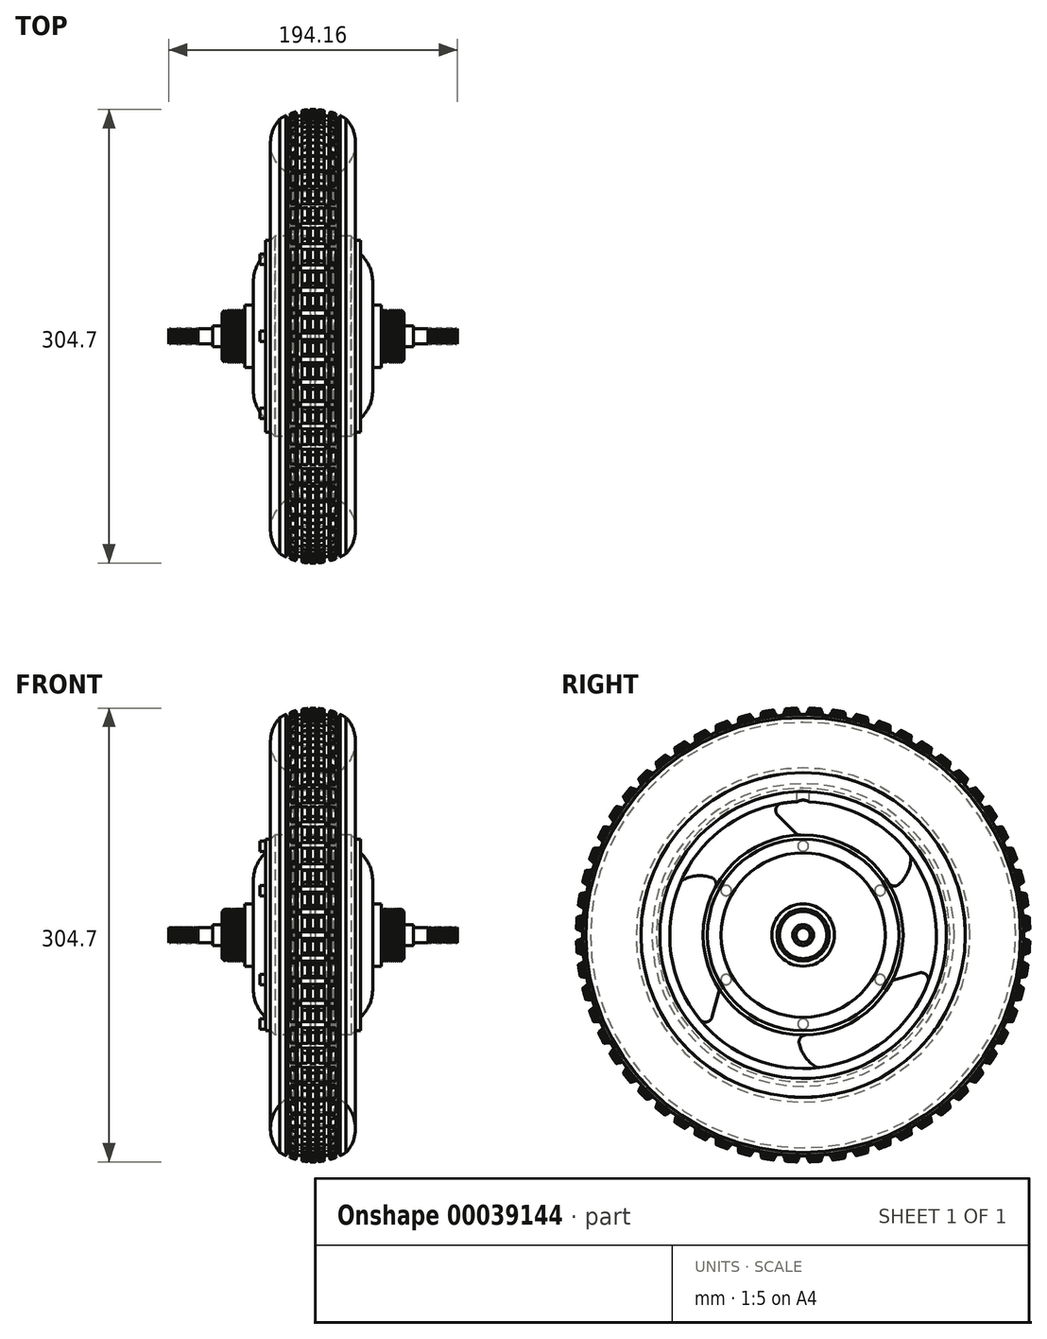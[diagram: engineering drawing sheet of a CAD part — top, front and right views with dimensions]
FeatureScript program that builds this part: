
annotation { "Feature Type Name" : "Feature", "Feature Type Description" : "" }
export const myFeature = defineFeature(function(context is Context, id is Id, definition is map)
    precondition{}
    {
        {
            var Q0;
            Q0=qCreatedBy(makeId("Front.planeOp"),FACE);
            var sketch = newSketch(context, id + "F0", { "sketchPlane" : qUnion([Q0])});
            skArc(sketch, "E0", {"start": v(0, 96.9) * mm, "mid": v(6.4, 97.33) * mm, "end": v(12.7, 98.63) * mm});
            skArc(sketch, "E1", {"start": v(18, 106.35) * mm, "mid": v(15.35, 109) * mm, "end": v(12.7, 106.35) * mm});
            skLineSegment(sketch, "E2", {"start": v(18, 106.35) * mm, "end": v(18, 96.3) * mm});
            skLineSegment(sketch, "E3", {"start": v(15.35, 109) * mm, "end": v(0, 109) * mm, "construction": true});
            skLineSegment(sketch, "E4", {"start": v(0, 0) * mm, "end": v(97.08, 0) * mm});
            skLineSegment(sketch, "E5", {"start": v(0, 0) * mm, "end": v(0, 109) * mm, "construction": true});
            skLineSegment(sketch, "E6", {"start": v(0, 96.9) * mm, "end": v(18, 96.9) * mm, "construction": true});
            skLineSegment(sketch, "E7", {"start": v(12.7, 98.63) * mm, "end": v(12.7, 106.35) * mm});
            skLineSegment(sketch, "E8", {"start": v(1.59, 67.19) * mm, "end": v(25.67, 67.19) * mm});
            skLineSegment(sketch, "E9", {"start": v(25.67, 67.19) * mm, "end": v(28.53, 64.33) * mm});
            skLineSegment(sketch, "E10", {"start": v(28.53, 64.33) * mm, "end": v(31.85, 64.33) * mm});
            skLineSegment(sketch, "E11", {"start": v(31.85, 64.33) * mm, "end": v(31.85, 55.2) * mm});
            skArc(sketch, "E12", {"start": v(40.1, 36.45) * mm, "mid": v(37.95, 46.7) * mm, "end": v(31.85, 55.2) * mm});
            skLineSegment(sketch, "E13", {"start": v(40.1, 36.45) * mm, "end": v(40.1, 20.94) * mm});
            skLineSegment(sketch, "E14", {"start": v(40.1, 20.94) * mm, "end": v(46, 20.94) * mm});
            skLineSegment(sketch, "E15", {"start": v(46, 20.94) * mm, "end": v(46, 17.46) * mm});
            skLineSegment(sketch, "E16", {"start": v(46, 17.46) * mm, "end": v(61, 17.46) * mm});
            skLineSegment(sketch, "E17", {"start": v(61, 17.46) * mm, "end": v(61, 7) * mm});
            skLineSegment(sketch, "E18", {"start": v(61, 7) * mm, "end": v(67.58, 7) * mm});
            skLineSegment(sketch, "E19", {"start": v(67.58, 7) * mm, "end": v(67.58, 5) * mm});
            skLineSegment(sketch, "E20", {"start": v(67.58, 5) * mm, "end": v(97.08, 5) * mm});
            skLineSegment(sketch, "E21", {"start": v(97.08, 5) * mm, "end": v(97.08, 0) * mm});
            skLineSegment(sketch, "E22", {"start": v(18, 96.3) * mm, "end": v(1.59, 89.65) * mm});
            skLineSegment(sketch, "E23", {"start": v(1.59, 89.65) * mm, "end": v(1.59, 67.18) * mm});
            skLineSegment(sketch, "E24.MirrorCS", {"start": v(-25.67, 67.18) * mm, "end": v(-28.53, 64.33) * mm});
            skLineSegment(sketch, "E25.MirrorCS", {"start": v(-67.58, 7) * mm, "end": v(-67.58, 5) * mm});
            skLineSegment(sketch, "E26.MirrorCS", {"start": v(-61, 7) * mm, "end": v(-67.58, 7) * mm});
            skLineSegment(sketch, "E27.MirrorCS", {"start": v(-12.7, 98.63) * mm, "end": v(-12.7, 106.35) * mm});
            skLineSegment(sketch, "E28.MirrorCS", {"start": v(-97.08, 5) * mm, "end": v(-97.08, 0) * mm});
            skLineSegment(sketch, "E29.MirrorCS", {"start": v(-40.1, 20.94) * mm, "end": v(-46, 20.94) * mm});
            skLineSegment(sketch, "E30.MirrorCS", {"start": v(-28.53, 64.33) * mm, "end": v(-31.85, 64.33) * mm});
            skLineSegment(sketch, "E31.MirrorCS", {"start": v(-46, 20.94) * mm, "end": v(-46, 17.46) * mm});
            skLineSegment(sketch, "E32.MirrorCS", {"start": v(-46, 17.46) * mm, "end": v(-61, 17.46) * mm});
            skLineSegment(sketch, "E33.MirrorCS", {"start": v(0, 96.9) * mm, "end": v(-18, 96.9) * mm, "construction": true});
            skLineSegment(sketch, "E34.MirrorCS", {"start": v(-18, 106.35) * mm, "end": v(-18, 96.3) * mm});
            skLineSegment(sketch, "E35.MirrorCS", {"start": v(-40.1, 36.45) * mm, "end": v(-40.1, 20.94) * mm});
            skArc(sketch, "E36.MirrorCS", {"start": v(-18, 106.35) * mm, "mid": v(-15.35, 109) * mm, "end": v(-12.7, 106.35) * mm});
            skLineSegment(sketch, "E37.MirrorCS", {"start": v(-61, 17.46) * mm, "end": v(-61, 7) * mm});
            skLineSegment(sketch, "E38.MirrorCS", {"start": v(-15.35, 109) * mm, "end": v(0, 109) * mm, "construction": true});
            skLineSegment(sketch, "E39.MirrorCS", {"start": v(0, 0) * mm, "end": v(-97.08, 0) * mm});
            skLineSegment(sketch, "E40.MirrorCS", {"start": v(-1.59, 67.19) * mm, "end": v(-25.67, 67.19) * mm});
            skLineSegment(sketch, "E41.MirrorCS", {"start": v(-18, 96.3) * mm, "end": v(-1.59, 89.65) * mm});
            skLineSegment(sketch, "E42.MirrorCS", {"start": v(-31.85, 64.33) * mm, "end": v(-31.85, 55.2) * mm});
            skLineSegment(sketch, "E43.MirrorCS", {"start": v(-1.59, 89.65) * mm, "end": v(-1.59, 67.18) * mm});
            skArc(sketch, "E44.MirrorCS", {"start": v(0, 96.9) * mm, "mid": v(-6.4, 97.33) * mm, "end": v(-12.7, 98.63) * mm});
            skLineSegment(sketch, "E45.MirrorCS", {"start": v(-67.58, 5) * mm, "end": v(-97.08, 5) * mm});
            skArc(sketch, "E46.MirrorCS", {"start": v(-40.1, 36.45) * mm, "mid": v(-37.95, 46.7) * mm, "end": v(-31.85, 55.2) * mm});
            skSolve(sketch);
        }
        {
            var Q0;
            Q0 = qSketchRegion(id + "F0", true);
            var Q1;
            Q1=sQuery(id+"F0.wireOp",EDGE,"E4");
            revolve(context, id + "F1", {"entities" : qUnion([Q0]), "axis" : qUnion([Q1]), "revolveType" : RevolveType.FULL});
        }
        {
            var Q0;
            Q0=makeQuery(id+"F1.opRevolve","SWEPT_FACE",FACE,{"disambiguationData":[OSD([sQuery(id+"F0.wireOp",EDGE,"E23")])]});
            var sketch = newSketch(context, id + "F2", { "sketchPlane" : qUnion([Q0])});
            skArc(sketch, "E47.0", {"start": v(-56.44, 36.45) * mm, "mid": v(-67.18, -0.2) * mm, "end": v(-56.23, -36.78) * mm});
            skArc(sketch, "E48.1", {"start": v(-63.4, -63.4) * mm, "mid": v(-88.15, -16.34) * mm, "end": v(-81.9, 36.45) * mm});
            skLineSegment(sketch, "E49", {"start": v(-36.5, 36.45) * mm, "end": v(-81.9, 36.45) * mm, "construction": true});
            skLineSegment(sketch, "E50", {"start": v(-63.4, -63.4) * mm, "end": v(-36.5, 36.45) * mm, "construction": true});
            skLineSegment(sketch, "E51", {"start": v(0, 0) * mm, "end": v(-63.4, -63.4) * mm, "construction": true});
            skArc(sketch, "E52", {"start": v(-56.44, 36.45) * mm, "mid": v(-69.17, 39.87) * mm, "end": v(-81.9, 36.45) * mm});
            skLineSegment(sketch, "E53", {"start": v(-63.4, -63.4) * mm, "end": v(-56.23, -36.78) * mm});
            skLineSegment(sketch, "E54.1.0", {"start": v(86.6, -23.2) * mm, "end": v(59.96, -30.3) * mm});
            skArc(sketch, "E54.1.1", {"start": v(-3.35, -67.1) * mm, "mid": v(0.06, -79.84) * mm, "end": v(9.39, -89.16) * mm});
            skArc(sketch, "E54.1.2", {"start": v(86.6, -23.2) * mm, "mid": v(58.23, -68.17) * mm, "end": v(9.39, -89.16) * mm});
            skArc(sketch, "E54.1.3", {"start": v(-3.35, -67.1) * mm, "mid": v(33.76, -58.09) * mm, "end": v(59.96, -30.3) * mm});
            skArc(sketch, "E54.1.4", {"start": v(-3.35, -67.1) * mm, "mid": v(33.76, -58.09) * mm, "end": v(59.96, -30.3) * mm});
            skLineSegment(sketch, "E54.2.0", {"start": v(-23.2, 86.6) * mm, "end": v(-3.74, 67.08) * mm});
            skArc(sketch, "E54.2.1", {"start": v(59.79, 30.65) * mm, "mid": v(69.12, 39.97) * mm, "end": v(72.52, 52.7) * mm});
            skArc(sketch, "E54.2.2", {"start": v(-23.2, 86.6) * mm, "mid": v(29.92, 84.51) * mm, "end": v(72.52, 52.7) * mm});
            skArc(sketch, "E54.2.3", {"start": v(59.79, 30.65) * mm, "mid": v(33.42, 58.28) * mm, "end": v(-3.74, 67.08) * mm});
            skArc(sketch, "E54.2.4", {"start": v(59.79, 30.65) * mm, "mid": v(33.42, 58.28) * mm, "end": v(-3.74, 67.08) * mm});
            skSolve(sketch);
        }
        {
            var Q0;
            Q0 = qSketchRegion(id + "F2", true);
            extrude(context, id + "F3", {"entities" : qUnion([Q0]), "operationType" : NewBodyOperationType.REMOVE, "endBound" : BoundingType.THROUGH_ALL, "oppositeDirection" : true, "depth" : 25.4 * mm});
        }
        {
            var Q0;
            Q0=makeQuery(id+"F3.boolean.opBoolean","COPY",EDGE,{"derivedFrom":makeQuery(id+"F3.opExtrude","SWEPT_EDGE",EDGE,{"disambiguationData":[OSD([sQuery(id+"F0.wireOp",EDGE,"E22"),sQuery(id+"F0.wireOp",EDGE,"E23"),sQuery(id+"F2.wireOp",EDGE,"E48.1"),sQuery(id+"F2.wireOp",EDGE,"E53")])]})});
            var Q1;
            Q1=makeQuery(id+"F3.boolean.opBoolean","COPY",EDGE,{"derivedFrom":makeQuery(id+"F3.opExtrude","SWEPT_EDGE",EDGE,{"disambiguationData":[OSD([sQuery(id+"F0.wireOp",EDGE,"E8"),sQuery(id+"F0.wireOp",EDGE,"E23"),sQuery(id+"F2.wireOp",EDGE,"E47.0"),sQuery(id+"F2.wireOp",EDGE,"E53")])]})});
            var Q2;
            Q2=makeQuery(id+"F3.boolean.opBoolean","COPY",EDGE,{"derivedFrom":makeQuery(id+"F3.opExtrude","SWEPT_EDGE",EDGE,{"disambiguationData":[OSD([sQuery(id+"F0.wireOp",EDGE,"E8"),sQuery(id+"F0.wireOp",EDGE,"E23"),sQuery(id+"F2.wireOp",EDGE,"E47.0"),sQuery(id+"F2.wireOp",EDGE,"E52")])]})});
            var Q3;
            Q3=makeQuery(id+"F3.boolean.opBoolean","COPY",EDGE,{"derivedFrom":makeQuery(id+"F3.opExtrude","SWEPT_EDGE",EDGE,{"disambiguationData":[OSD([sQuery(id+"F0.wireOp",EDGE,"E22"),sQuery(id+"F0.wireOp",EDGE,"E23"),sQuery(id+"F2.wireOp",EDGE,"E48.1"),sQuery(id+"F2.wireOp",EDGE,"E52")])]})});
            var Q4;
            Q4=makeQuery(id+"F3.boolean.opBoolean","COPY",EDGE,{"derivedFrom":makeQuery(id+"F3.opExtrude","SWEPT_EDGE",EDGE,{"disambiguationData":[OSD([sQuery(id+"F0.wireOp",EDGE,"E22"),sQuery(id+"F0.wireOp",EDGE,"E23"),sQuery(id+"F2.wireOp",EDGE,"E54.1.1"),sQuery(id+"F2.wireOp",EDGE,"E54.1.2")])]})});
            var Q5;
            Q5=makeQuery(id+"F3.boolean.opBoolean","COPY",EDGE,{"derivedFrom":makeQuery(id+"F3.opExtrude","SWEPT_EDGE",EDGE,{"disambiguationData":[OSD([sQuery(id+"F0.wireOp",EDGE,"E8"),sQuery(id+"F0.wireOp",EDGE,"E23"),sQuery(id+"F2.wireOp",EDGE,"E54.1.1"),sQuery(id+"F2.wireOp",EDGE,"E54.1.4")])]})});
            var Q6;
            Q6=makeQuery(id+"F3.boolean.opBoolean","COPY",EDGE,{"derivedFrom":makeQuery(id+"F3.opExtrude","SWEPT_EDGE",EDGE,{"disambiguationData":[OSD([sQuery(id+"F0.wireOp",EDGE,"E22"),sQuery(id+"F0.wireOp",EDGE,"E23"),sQuery(id+"F2.wireOp",EDGE,"E54.1.0"),sQuery(id+"F2.wireOp",EDGE,"E54.1.2")])]})});
            var Q7;
            Q7=makeQuery(id+"F3.boolean.opBoolean","COPY",EDGE,{"derivedFrom":makeQuery(id+"F3.opExtrude","SWEPT_EDGE",EDGE,{"disambiguationData":[OSD([sQuery(id+"F0.wireOp",EDGE,"E8"),sQuery(id+"F0.wireOp",EDGE,"E23"),sQuery(id+"F2.wireOp",EDGE,"E54.1.0"),sQuery(id+"F2.wireOp",EDGE,"E54.1.4")])]})});
            var Q8;
            Q8=makeQuery(id+"F3.boolean.opBoolean","COPY",EDGE,{"derivedFrom":makeQuery(id+"F3.opExtrude","SWEPT_EDGE",EDGE,{"disambiguationData":[OSD([sQuery(id+"F0.wireOp",EDGE,"E8"),sQuery(id+"F0.wireOp",EDGE,"E23"),sQuery(id+"F2.wireOp",EDGE,"E54.2.1"),sQuery(id+"F2.wireOp",EDGE,"E54.2.4")])]})});
            var Q9;
            Q9=makeQuery(id+"F3.boolean.opBoolean","COPY",EDGE,{"derivedFrom":makeQuery(id+"F3.opExtrude","SWEPT_EDGE",EDGE,{"disambiguationData":[OSD([sQuery(id+"F0.wireOp",EDGE,"E22"),sQuery(id+"F0.wireOp",EDGE,"E23"),sQuery(id+"F2.wireOp",EDGE,"E54.2.1"),sQuery(id+"F2.wireOp",EDGE,"E54.2.2")])]})});
            var Q10;
            Q10=makeQuery(id+"F3.boolean.opBoolean","COPY",EDGE,{"derivedFrom":makeQuery(id+"F3.opExtrude","SWEPT_EDGE",EDGE,{"disambiguationData":[OSD([sQuery(id+"F0.wireOp",EDGE,"E8"),sQuery(id+"F0.wireOp",EDGE,"E23"),sQuery(id+"F2.wireOp",EDGE,"E54.2.0"),sQuery(id+"F2.wireOp",EDGE,"E54.2.4")])]})});
            var Q11;
            Q11=makeQuery(id+"F3.boolean.opBoolean","COPY",EDGE,{"derivedFrom":makeQuery(id+"F3.opExtrude","SWEPT_EDGE",EDGE,{"disambiguationData":[OSD([sQuery(id+"F0.wireOp",EDGE,"E22"),sQuery(id+"F0.wireOp",EDGE,"E23"),sQuery(id+"F2.wireOp",EDGE,"E54.2.0"),sQuery(id+"F2.wireOp",EDGE,"E54.2.2")])]})});
            fillet(context, id + "F4", {"entities" : qUnion([Q0, Q1, Q2, Q3, Q4, Q5, Q6, Q7, Q8, Q9, Q10, Q11]), "radius" : 4.76 * mm, "tangentPropagation" : true, "allowEdgeOverflow" : false});
        }
        {
            var Q0;
            Q0=qCreatedBy(makeId("Top.planeOp"),FACE);
            cPlane(context, id + "F5", {"entities" : qUnion([Q0]), "cplaneType" : CPlaneType.OFFSET, "offset" : 114.3 * mm, "width" : 152.4 * mm, "height" : 152.4 * mm});
        }
        {
            var Q0;
            Q0=qCreatedBy(id+"F5.planeOp",FACE);
            var sketch = newSketch(context, id + "F6", { "sketchPlane" : qUnion([Q0])});
            skCircle(sketch, "E55", {"center": v(0, 0) * mm, "radius": 4 * mm});
            skSolve(sketch);
        }
        {
            var Q0;
            Q0=makeQuery(id+"F6.imprint","IMPRINT",FACE,{"disambiguationData":[TD([[makeQuery(id+"F6.imprint","IMPRINT",EDGE,{"derivedFrom":sQuery(id+"F6.wireOp",EDGE,"E55")}),1.0]])]});
            extrude(context, id + "F7", {"entities" : qUnion([Q0]), "operationType" : NewBodyOperationType.REMOVE, "oppositeDirection" : true, "depth" : 38.1 * mm});
        }
        {
            var Q0;
            Q0=makeQuery(id+"F1.opRevolve","SWEPT_FACE",FACE,{"disambiguationData":[OSD([sQuery(id+"F0.wireOp",EDGE,"E42.MirrorCS")])]});
            var sketch = newSketch(context, id + "F8", { "sketchPlane" : qUnion([Q0])});
            skCircle(sketch, "E56", {"center": v(0, 59.76) * mm, "radius": 3.5 * mm});
            skLineSegment(sketch, "E57", {"start": v(0, 64.33) * mm, "end": v(0, 55.2) * mm, "construction": true});
            skCircle(sketch, "E58.1.0", {"center": v(-51.76, 29.88) * mm, "radius": 3.5 * mm});
            skCircle(sketch, "E58.2.0", {"center": v(-51.76, -29.88) * mm, "radius": 3.5 * mm});
            skCircle(sketch, "E58.3.0", {"center": v(0, -59.76) * mm, "radius": 3.5 * mm});
            skCircle(sketch, "E58.4.0", {"center": v(51.76, -29.88) * mm, "radius": 3.5 * mm});
            skCircle(sketch, "E58.5.0", {"center": v(51.76, 29.88) * mm, "radius": 3.5 * mm});
            skPoint(sketch, "E58.center", {"position": v(0, 0) * mm});
            skSolve(sketch);
        }
        {
            var Q0;
            Q0=makeQuery(id+"F1.opRevolve","SWEPT_EDGE",EDGE,{"disambiguationData":[OSD([sQuery(id+"F0.wireOp",EDGE,"E16"),sQuery(id+"F0.wireOp",EDGE,"E17")])]});
            var Q1;
            Q1=makeQuery(id+"F1.opRevolve","SWEPT_EDGE",EDGE,{"disambiguationData":[OSD([sQuery(id+"F0.wireOp",EDGE,"E32.MirrorCS"),sQuery(id+"F0.wireOp",EDGE,"E37.MirrorCS")])]});
            chamfer(context, id + "F9", {"entities" : qUnion([Q0, Q1]), "width" : 1.59 * mm, "tangentPropagation" : true});
        }
        {
            var Q0;
            Q0 = qSketchRegion(id + "F8", true);
            extrude(context, id + "F10", {"entities" : qUnion([Q0]), "operationType" : NewBodyOperationType.ADD, "depth" : 3.7 * mm});
        }
        {
            var Q0;
            Q0=qCreatedBy(makeId("Front.planeOp"),FACE);
            var sketch = newSketch(context, id + "F11", { "sketchPlane" : qUnion([Q0])});
            skLineSegment(sketch, "E59", {"start": v(12.7, 101.6) * mm, "end": v(12.7, 109) * mm});
            skLineSegment(sketch, "E60", {"start": v(12.7, 109) * mm, "end": v(15.88, 109) * mm});
            skArc(sketch, "E61", {"start": v(15.87, 109) * mm, "mid": v(28.24, 125.95) * mm, "end": v(22.23, 146.05) * mm});
            skArc(sketch, "E62", {"start": v(22.23, 146.05) * mm, "mid": v(20.29, 147.18) * mm, "end": v(18.3, 148.21) * mm});
            skLineSegment(sketch, "E63", {"start": v(0, 152.4) * mm, "end": v(22.23, 152.4) * mm, "construction": true});
            skLineSegment(sketch, "E64", {"start": v(12.7, 101.6) * mm, "end": v(9.53, 101.6) * mm});
            skLineSegment(sketch, "E65", {"start": v(9.53, 101.6) * mm, "end": v(9.53, 112.17) * mm});
            skLineSegment(sketch, "E66", {"start": v(9.53, 112.17) * mm, "end": v(15.88, 112.17) * mm});
            skLineSegment(sketch, "E67", {"start": v(15.88, 112.17) * mm, "end": v(15.88, 142.88) * mm});
            skLineSegment(sketch, "E68", {"start": v(15.88, 142.88) * mm, "end": v(0, 142.88) * mm});
            skLineSegment(sketch, "E69", {"start": v(0, 152.4) * mm, "end": v(0, 142.88) * mm, "construction": true});
            skLineSegment(sketch, "E70", {"start": v(97.43, 0) * mm, "end": v(-97.61, 0) * mm, "construction": true});
            skLineSegment(sketch, "E71", {"start": v(28.58, 0) * mm, "end": v(28.58, 152.4) * mm, "construction": true});
            skLineSegment(sketch, "E72", {"start": v(0, 0) * mm, "end": v(0, 110.33) * mm, "construction": true});
            skLineSegment(sketch, "E73.MirrorCS", {"start": v(-12.7, 109) * mm, "end": v(-15.88, 109) * mm});
            skLineSegment(sketch, "E74.MirrorCS", {"start": v(-12.7, 101.6) * mm, "end": v(-9.53, 101.6) * mm});
            skLineSegment(sketch, "E75.MirrorCS", {"start": v(-12.7, 101.6) * mm, "end": v(-12.7, 109) * mm});
            skLineSegment(sketch, "E76.MirrorCS", {"start": v(-15.88, 112.17) * mm, "end": v(-15.88, 142.88) * mm});
            skLineSegment(sketch, "E77.MirrorCS", {"start": v(-15.88, 142.88) * mm, "end": v(0, 142.88) * mm});
            skLineSegment(sketch, "E78.MirrorCS", {"start": v(-9.53, 112.17) * mm, "end": v(-15.88, 112.17) * mm});
            skArc(sketch, "E79.MirrorCS", {"start": v(-22.23, 146.05) * mm, "mid": v(-20.29, 147.18) * mm, "end": v(-18.3, 148.21) * mm});
            skArc(sketch, "E80.MirrorCS", {"start": v(-15.87, 109) * mm, "mid": v(-28.24, 125.95) * mm, "end": v(-22.23, 146.05) * mm});
            skLineSegment(sketch, "E81.MirrorCS", {"start": v(0, 152.4) * mm, "end": v(-22.23, 152.4) * mm, "construction": true});
            skLineSegment(sketch, "E82.MirrorCS", {"start": v(-9.53, 101.6) * mm, "end": v(-9.53, 112.17) * mm});
            skLineSegment(sketch, "E83", {"start": v(18.3, 148.21) * mm, "end": v(17.04, 145.7) * mm});
            skLineSegment(sketch, "E84", {"start": v(17.04, 145.7) * mm, "end": v(14.16, 147.13) * mm});
            skLineSegment(sketch, "E85", {"start": v(14.16, 147.13) * mm, "end": v(15.34, 149.5) * mm});
            skLineSegment(sketch, "E86", {"start": v(11.56, 150.78) * mm, "end": v(10.63, 147.58) * mm});
            skLineSegment(sketch, "E87", {"start": v(10.63, 147.58) * mm, "end": v(7.33, 148.54) * mm});
            skLineSegment(sketch, "E88", {"start": v(7.33, 148.54) * mm, "end": v(7.33, 151.76) * mm});
            skLineSegment(sketch, "E89", {"start": v(3.73, 152.23) * mm, "end": v(3.73, 149.03) * mm});
            skLineSegment(sketch, "E90", {"start": v(3.73, 149.03) * mm, "end": v(1.73, 149.03) * mm});
            skLineSegment(sketch, "E91", {"start": v(1.73, 149.03) * mm, "end": v(1.73, 152.4) * mm});
            skArc(sketch, "E92.trimOffspring", {"start": v(15.34, 149.5) * mm, "mid": v(13.47, 150.19) * mm, "end": v(11.56, 150.78) * mm});
            skArc(sketch, "E93.trimOffspring", {"start": v(7.33, 151.76) * mm, "mid": v(5.54, 152.03) * mm, "end": v(3.73, 152.23) * mm});
            skArc(sketch, "E94.trimOffspring", {"start": v(1.73, 152.36) * mm, "mid": v(0.87, 152.4) * mm, "end": v(0, 152.4) * mm});
            skLineSegment(sketch, "E95.MirrorCS", {"start": v(-18.3, 148.21) * mm, "end": v(-17.04, 145.7) * mm});
            skLineSegment(sketch, "E96.MirrorCS", {"start": v(-17.04, 145.7) * mm, "end": v(-14.16, 147.13) * mm});
            skLineSegment(sketch, "E97.MirrorCS", {"start": v(-14.16, 147.13) * mm, "end": v(-15.34, 149.5) * mm});
            skLineSegment(sketch, "E98.MirrorCS", {"start": v(-11.56, 150.78) * mm, "end": v(-10.63, 147.58) * mm});
            skLineSegment(sketch, "E99.MirrorCS", {"start": v(-10.63, 147.58) * mm, "end": v(-7.33, 148.54) * mm});
            skLineSegment(sketch, "E100.MirrorCS", {"start": v(-7.33, 148.54) * mm, "end": v(-7.33, 151.76) * mm});
            skLineSegment(sketch, "E101.MirrorCS", {"start": v(-3.73, 152.23) * mm, "end": v(-3.73, 149.03) * mm});
            skLineSegment(sketch, "E102.MirrorCS", {"start": v(-3.73, 149.03) * mm, "end": v(-1.73, 149.03) * mm});
            skLineSegment(sketch, "E103.MirrorCS", {"start": v(-1.73, 149.03) * mm, "end": v(-1.73, 152.4) * mm});
            skArc(sketch, "E104.trimOffspring", {"start": v(-1.73, 152.36) * mm, "mid": v(-0.87, 152.4) * mm, "end": v(0, 152.4) * mm});
            skArc(sketch, "E105.trimOffspring", {"start": v(-7.33, 151.76) * mm, "mid": v(-5.54, 152.03) * mm, "end": v(-3.73, 152.23) * mm});
            skArc(sketch, "E106.trimOffspring", {"start": v(-15.34, 149.5) * mm, "mid": v(-13.47, 150.19) * mm, "end": v(-11.56, 150.78) * mm});
            skSolve(sketch);
        }
        {
            var Q0;
            Q0 = qSketchRegion(id + "F11", true);
            var Q1;
            Q1=sQuery(id+"F11.wireOp",EDGE,"E70");
            revolve(context, id + "F12", {"entities" : qUnion([Q0]), "axis" : qUnion([Q1]), "revolveType" : RevolveType.FULL});
        }
        {
            var Q0;
            Q0=qCreatedBy(makeId("Right.planeOp"),FACE);
            var sketch = newSketch(context, id + "F13", { "sketchPlane" : qUnion([Q0])});
            skLineSegment(sketch, "E107", {"start": v(0, 152.6) * mm, "end": v(0, 148.21) * mm, "construction": true});
            skLineSegment(sketch, "E108", {"start": v(0, 148.21) * mm, "end": v(-2.17, 148.21) * mm});
            skLineSegment(sketch, "E109", {"start": v(-2.17, 148.21) * mm, "end": v(-4.53, 153.56) * mm});
            skLineSegment(sketch, "E110", {"start": v(-4.53, 153.56) * mm, "end": v(0, 152.6) * mm});
            skLineSegment(sketch, "E111.MirrorCS", {"start": v(0, 148.21) * mm, "end": v(2.17, 148.21) * mm});
            skLineSegment(sketch, "E112.MirrorCS", {"start": v(2.17, 148.21) * mm, "end": v(4.53, 153.56) * mm});
            skLineSegment(sketch, "E113.MirrorCS", {"start": v(4.53, 153.56) * mm, "end": v(0, 152.6) * mm});
            skLineSegment(sketch, "E114.1.0", {"start": v(-15.95, 151.76) * mm, "end": v(-15.5, 147.4) * mm, "construction": true});
            skLineSegment(sketch, "E114.1.1", {"start": v(-13.33, 147.63) * mm, "end": v(-11.54, 153.2) * mm});
            skLineSegment(sketch, "E114.1.2", {"start": v(-11.54, 153.2) * mm, "end": v(-15.95, 151.76) * mm});
            skLineSegment(sketch, "E114.1.3", {"start": v(-15.5, 147.4) * mm, "end": v(-13.33, 147.63) * mm});
            skLineSegment(sketch, "E114.1.4", {"start": v(-17.65, 147.18) * mm, "end": v(-20.56, 152.24) * mm});
            skLineSegment(sketch, "E114.1.5", {"start": v(-20.56, 152.24) * mm, "end": v(-15.95, 151.76) * mm});
            skLineSegment(sketch, "E114.1.6", {"start": v(-15.5, 147.4) * mm, "end": v(-17.65, 147.18) * mm});
            skLineSegment(sketch, "E114.2.0", {"start": v(-31.73, 149.26) * mm, "end": v(-30.82, 144.98) * mm, "construction": true});
            skLineSegment(sketch, "E114.2.1", {"start": v(-28.69, 145.43) * mm, "end": v(-27.5, 151.14) * mm});
            skLineSegment(sketch, "E114.2.2", {"start": v(-27.5, 151.14) * mm, "end": v(-31.73, 149.26) * mm});
            skLineSegment(sketch, "E114.2.3", {"start": v(-30.82, 144.98) * mm, "end": v(-28.69, 145.43) * mm});
            skLineSegment(sketch, "E114.2.4", {"start": v(-32.94, 144.52) * mm, "end": v(-36.36, 149.26) * mm});
            skLineSegment(sketch, "E114.2.5", {"start": v(-36.36, 149.26) * mm, "end": v(-31.73, 149.26) * mm});
            skLineSegment(sketch, "E114.2.6", {"start": v(-30.82, 144.98) * mm, "end": v(-32.94, 144.52) * mm});
            skLineSegment(sketch, "E114.3.0", {"start": v(-47.16, 145.13) * mm, "end": v(-45.8, 140.96) * mm, "construction": true});
            skLineSegment(sketch, "E114.3.1", {"start": v(-43.73, 141.63) * mm, "end": v(-43.14, 147.44) * mm});
            skLineSegment(sketch, "E114.3.2", {"start": v(-43.14, 147.44) * mm, "end": v(-47.16, 145.13) * mm});
            skLineSegment(sketch, "E114.3.3", {"start": v(-45.8, 140.96) * mm, "end": v(-43.73, 141.63) * mm});
            skLineSegment(sketch, "E114.3.4", {"start": v(-47.87, 140.29) * mm, "end": v(-51.76, 144.64) * mm});
            skLineSegment(sketch, "E114.3.5", {"start": v(-51.76, 144.64) * mm, "end": v(-47.16, 145.13) * mm});
            skLineSegment(sketch, "E114.3.6", {"start": v(-45.8, 140.96) * mm, "end": v(-47.87, 140.29) * mm});
            skLineSegment(sketch, "E114.4.0", {"start": v(-62.07, 139.4) * mm, "end": v(-60.28, 135.4) * mm, "construction": true});
            skLineSegment(sketch, "E114.4.1", {"start": v(-58.3, 136.29) * mm, "end": v(-58.32, 142.13) * mm});
            skLineSegment(sketch, "E114.4.2", {"start": v(-58.32, 142.13) * mm, "end": v(-62.07, 139.4) * mm});
            skLineSegment(sketch, "E114.4.3", {"start": v(-60.28, 135.4) * mm, "end": v(-58.3, 136.29) * mm});
            skLineSegment(sketch, "E114.4.4", {"start": v(-62.27, 134.52) * mm, "end": v(-66.6, 138.44) * mm});
            skLineSegment(sketch, "E114.4.5", {"start": v(-66.6, 138.44) * mm, "end": v(-62.07, 139.4) * mm});
            skLineSegment(sketch, "E114.4.6", {"start": v(-60.28, 135.4) * mm, "end": v(-62.27, 134.52) * mm});
            skLineSegment(sketch, "E114.5.0", {"start": v(-76.3, 132.15) * mm, "end": v(-74.1, 128.36) * mm, "construction": true});
            skLineSegment(sketch, "E114.5.1", {"start": v(-72.22, 129.44) * mm, "end": v(-72.85, 135.25) * mm});
            skLineSegment(sketch, "E114.5.2", {"start": v(-72.85, 135.25) * mm, "end": v(-76.3, 132.15) * mm});
            skLineSegment(sketch, "E114.5.3", {"start": v(-74.1, 128.36) * mm, "end": v(-72.22, 129.44) * mm});
            skLineSegment(sketch, "E114.5.4", {"start": v(-76, 127.27) * mm, "end": v(-80.7, 130.72) * mm});
            skLineSegment(sketch, "E114.5.5", {"start": v(-80.7, 130.72) * mm, "end": v(-76.3, 132.15) * mm});
            skLineSegment(sketch, "E114.5.6", {"start": v(-74.1, 128.36) * mm, "end": v(-76, 127.27) * mm});
            skLineSegment(sketch, "E114.6.0", {"start": v(-89.7, 123.45) * mm, "end": v(-87.12, 119.9) * mm, "construction": true});
            skLineSegment(sketch, "E114.6.1", {"start": v(-85.36, 121.19) * mm, "end": v(-86.6, 126.9) * mm});
            skLineSegment(sketch, "E114.6.2", {"start": v(-86.6, 126.9) * mm, "end": v(-89.7, 123.45) * mm});
            skLineSegment(sketch, "E114.6.3", {"start": v(-87.12, 119.9) * mm, "end": v(-85.36, 121.19) * mm});
            skLineSegment(sketch, "E114.6.4", {"start": v(-88.88, 118.63) * mm, "end": v(-93.93, 121.57) * mm});
            skLineSegment(sketch, "E114.6.5", {"start": v(-93.93, 121.57) * mm, "end": v(-89.7, 123.45) * mm});
            skLineSegment(sketch, "E114.6.6", {"start": v(-87.12, 119.9) * mm, "end": v(-88.88, 118.63) * mm});
            skLineSegment(sketch, "E114.7.0", {"start": v(-102.1, 113.4) * mm, "end": v(-99.17, 110.14) * mm, "construction": true});
            skLineSegment(sketch, "E114.7.1", {"start": v(-97.56, 111.6) * mm, "end": v(-99.38, 117.15) * mm});
            skLineSegment(sketch, "E114.7.2", {"start": v(-99.38, 117.15) * mm, "end": v(-102.1, 113.4) * mm});
            skLineSegment(sketch, "E114.7.3", {"start": v(-99.17, 110.14) * mm, "end": v(-97.56, 111.6) * mm});
            skLineSegment(sketch, "E114.7.4", {"start": v(-100.8, 108.7) * mm, "end": v(-106.12, 111.08) * mm});
            skLineSegment(sketch, "E114.7.5", {"start": v(-106.12, 111.08) * mm, "end": v(-102.1, 113.4) * mm});
            skLineSegment(sketch, "E114.7.6", {"start": v(-99.17, 110.14) * mm, "end": v(-100.8, 108.7) * mm});
            skLineSegment(sketch, "E114.8.0", {"start": v(-113.4, 102.1) * mm, "end": v(-110.14, 99.17) * mm, "construction": true});
            skLineSegment(sketch, "E114.8.1", {"start": v(-108.7, 100.8) * mm, "end": v(-111.08, 106.12) * mm});
            skLineSegment(sketch, "E114.8.2", {"start": v(-111.08, 106.12) * mm, "end": v(-113.4, 102.1) * mm});
            skLineSegment(sketch, "E114.8.3", {"start": v(-110.14, 99.17) * mm, "end": v(-108.7, 100.8) * mm});
            skLineSegment(sketch, "E114.8.4", {"start": v(-111.6, 97.56) * mm, "end": v(-117.15, 99.38) * mm});
            skLineSegment(sketch, "E114.8.5", {"start": v(-117.15, 99.38) * mm, "end": v(-113.4, 102.1) * mm});
            skLineSegment(sketch, "E114.8.6", {"start": v(-110.14, 99.17) * mm, "end": v(-111.6, 97.56) * mm});
            skLineSegment(sketch, "E114.9.0", {"start": v(-123.45, 89.7) * mm, "end": v(-119.9, 87.12) * mm, "construction": true});
            skLineSegment(sketch, "E114.9.1", {"start": v(-118.63, 88.88) * mm, "end": v(-121.57, 93.93) * mm});
            skLineSegment(sketch, "E114.9.2", {"start": v(-121.57, 93.93) * mm, "end": v(-123.45, 89.7) * mm});
            skLineSegment(sketch, "E114.9.3", {"start": v(-119.9, 87.12) * mm, "end": v(-118.63, 88.88) * mm});
            skLineSegment(sketch, "E114.9.4", {"start": v(-121.19, 85.36) * mm, "end": v(-126.9, 86.6) * mm});
            skLineSegment(sketch, "E114.9.5", {"start": v(-126.9, 86.6) * mm, "end": v(-123.45, 89.7) * mm});
            skLineSegment(sketch, "E114.9.6", {"start": v(-119.9, 87.12) * mm, "end": v(-121.19, 85.36) * mm});
            skLineSegment(sketch, "E114.10.0", {"start": v(-132.15, 76.3) * mm, "end": v(-128.36, 74.1) * mm, "construction": true});
            skLineSegment(sketch, "E114.10.1", {"start": v(-127.27, 76) * mm, "end": v(-130.72, 80.7) * mm});
            skLineSegment(sketch, "E114.10.2", {"start": v(-130.72, 80.7) * mm, "end": v(-132.15, 76.3) * mm});
            skLineSegment(sketch, "E114.10.3", {"start": v(-128.36, 74.1) * mm, "end": v(-127.27, 76) * mm});
            skLineSegment(sketch, "E114.10.4", {"start": v(-129.44, 72.22) * mm, "end": v(-135.25, 72.85) * mm});
            skLineSegment(sketch, "E114.10.5", {"start": v(-135.25, 72.85) * mm, "end": v(-132.15, 76.3) * mm});
            skLineSegment(sketch, "E114.10.6", {"start": v(-128.36, 74.1) * mm, "end": v(-129.44, 72.22) * mm});
            skLineSegment(sketch, "E114.11.0", {"start": v(-139.4, 62.07) * mm, "end": v(-135.4, 60.28) * mm, "construction": true});
            skLineSegment(sketch, "E114.11.1", {"start": v(-134.52, 62.27) * mm, "end": v(-138.44, 66.6) * mm});
            skLineSegment(sketch, "E114.11.2", {"start": v(-138.44, 66.6) * mm, "end": v(-139.4, 62.07) * mm});
            skLineSegment(sketch, "E114.11.3", {"start": v(-135.4, 60.28) * mm, "end": v(-134.52, 62.27) * mm});
            skLineSegment(sketch, "E114.11.4", {"start": v(-136.29, 58.3) * mm, "end": v(-142.13, 58.32) * mm});
            skLineSegment(sketch, "E114.11.5", {"start": v(-142.13, 58.32) * mm, "end": v(-139.4, 62.07) * mm});
            skLineSegment(sketch, "E114.11.6", {"start": v(-135.4, 60.28) * mm, "end": v(-136.29, 58.3) * mm});
            skLineSegment(sketch, "E114.12.0", {"start": v(-145.13, 47.16) * mm, "end": v(-140.96, 45.8) * mm, "construction": true});
            skLineSegment(sketch, "E114.12.1", {"start": v(-140.29, 47.87) * mm, "end": v(-144.64, 51.76) * mm});
            skLineSegment(sketch, "E114.12.2", {"start": v(-144.64, 51.76) * mm, "end": v(-145.13, 47.16) * mm});
            skLineSegment(sketch, "E114.12.3", {"start": v(-140.96, 45.8) * mm, "end": v(-140.29, 47.87) * mm});
            skLineSegment(sketch, "E114.12.4", {"start": v(-141.63, 43.73) * mm, "end": v(-147.44, 43.14) * mm});
            skLineSegment(sketch, "E114.12.5", {"start": v(-147.44, 43.14) * mm, "end": v(-145.13, 47.16) * mm});
            skLineSegment(sketch, "E114.12.6", {"start": v(-140.96, 45.8) * mm, "end": v(-141.63, 43.73) * mm});
            skLineSegment(sketch, "E114.13.0", {"start": v(-149.26, 31.73) * mm, "end": v(-144.98, 30.82) * mm, "construction": true});
            skLineSegment(sketch, "E114.13.1", {"start": v(-144.52, 32.94) * mm, "end": v(-149.26, 36.36) * mm});
            skLineSegment(sketch, "E114.13.2", {"start": v(-149.26, 36.36) * mm, "end": v(-149.26, 31.73) * mm});
            skLineSegment(sketch, "E114.13.3", {"start": v(-144.98, 30.82) * mm, "end": v(-144.52, 32.94) * mm});
            skLineSegment(sketch, "E114.13.4", {"start": v(-145.43, 28.69) * mm, "end": v(-151.14, 27.5) * mm});
            skLineSegment(sketch, "E114.13.5", {"start": v(-151.14, 27.5) * mm, "end": v(-149.26, 31.73) * mm});
            skLineSegment(sketch, "E114.13.6", {"start": v(-144.98, 30.82) * mm, "end": v(-145.43, 28.69) * mm});
            skLineSegment(sketch, "E114.14.0", {"start": v(-151.76, 15.95) * mm, "end": v(-147.4, 15.5) * mm, "construction": true});
            skLineSegment(sketch, "E114.14.1", {"start": v(-147.18, 17.65) * mm, "end": v(-152.24, 20.56) * mm});
            skLineSegment(sketch, "E114.14.2", {"start": v(-152.24, 20.56) * mm, "end": v(-151.76, 15.95) * mm});
            skLineSegment(sketch, "E114.14.3", {"start": v(-147.4, 15.5) * mm, "end": v(-147.18, 17.65) * mm});
            skLineSegment(sketch, "E114.14.4", {"start": v(-147.63, 13.33) * mm, "end": v(-153.2, 11.54) * mm});
            skLineSegment(sketch, "E114.14.5", {"start": v(-153.2, 11.54) * mm, "end": v(-151.76, 15.95) * mm});
            skLineSegment(sketch, "E114.14.6", {"start": v(-147.4, 15.5) * mm, "end": v(-147.63, 13.33) * mm});
            skLineSegment(sketch, "E114.15.0", {"start": v(-152.6, 0) * mm, "end": v(-148.21, 0) * mm, "construction": true});
            skLineSegment(sketch, "E114.15.1", {"start": v(-148.21, 2.17) * mm, "end": v(-153.56, 4.53) * mm});
            skLineSegment(sketch, "E114.15.2", {"start": v(-153.56, 4.53) * mm, "end": v(-152.6, 0) * mm});
            skLineSegment(sketch, "E114.15.3", {"start": v(-148.21, 0) * mm, "end": v(-148.21, 2.17) * mm});
            skLineSegment(sketch, "E114.15.4", {"start": v(-148.21, -2.17) * mm, "end": v(-153.56, -4.53) * mm});
            skLineSegment(sketch, "E114.15.5", {"start": v(-153.56, -4.53) * mm, "end": v(-152.6, 0) * mm});
            skLineSegment(sketch, "E114.15.6", {"start": v(-148.21, 0) * mm, "end": v(-148.21, -2.17) * mm});
            skLineSegment(sketch, "E114.16.0", {"start": v(-151.76, -15.95) * mm, "end": v(-147.4, -15.5) * mm, "construction": true});
            skLineSegment(sketch, "E114.16.1", {"start": v(-147.63, -13.33) * mm, "end": v(-153.2, -11.54) * mm});
            skLineSegment(sketch, "E114.16.2", {"start": v(-153.2, -11.54) * mm, "end": v(-151.76, -15.95) * mm});
            skLineSegment(sketch, "E114.16.3", {"start": v(-147.4, -15.5) * mm, "end": v(-147.63, -13.33) * mm});
            skLineSegment(sketch, "E114.16.4", {"start": v(-147.18, -17.65) * mm, "end": v(-152.24, -20.56) * mm});
            skLineSegment(sketch, "E114.16.5", {"start": v(-152.24, -20.56) * mm, "end": v(-151.76, -15.95) * mm});
            skLineSegment(sketch, "E114.16.6", {"start": v(-147.4, -15.5) * mm, "end": v(-147.18, -17.65) * mm});
            skLineSegment(sketch, "E114.17.0", {"start": v(-149.26, -31.73) * mm, "end": v(-144.98, -30.82) * mm, "construction": true});
            skLineSegment(sketch, "E114.17.1", {"start": v(-145.43, -28.69) * mm, "end": v(-151.14, -27.5) * mm});
            skLineSegment(sketch, "E114.17.2", {"start": v(-151.14, -27.5) * mm, "end": v(-149.26, -31.73) * mm});
            skLineSegment(sketch, "E114.17.3", {"start": v(-144.98, -30.82) * mm, "end": v(-145.43, -28.69) * mm});
            skLineSegment(sketch, "E114.17.4", {"start": v(-144.52, -32.94) * mm, "end": v(-149.26, -36.36) * mm});
            skLineSegment(sketch, "E114.17.5", {"start": v(-149.26, -36.36) * mm, "end": v(-149.26, -31.73) * mm});
            skLineSegment(sketch, "E114.17.6", {"start": v(-144.98, -30.82) * mm, "end": v(-144.52, -32.94) * mm});
            skLineSegment(sketch, "E114.18.0", {"start": v(-145.13, -47.16) * mm, "end": v(-140.96, -45.8) * mm, "construction": true});
            skLineSegment(sketch, "E114.18.1", {"start": v(-141.63, -43.73) * mm, "end": v(-147.44, -43.14) * mm});
            skLineSegment(sketch, "E114.18.2", {"start": v(-147.44, -43.14) * mm, "end": v(-145.13, -47.16) * mm});
            skLineSegment(sketch, "E114.18.3", {"start": v(-140.96, -45.8) * mm, "end": v(-141.63, -43.73) * mm});
            skLineSegment(sketch, "E114.18.4", {"start": v(-140.29, -47.87) * mm, "end": v(-144.64, -51.76) * mm});
            skLineSegment(sketch, "E114.18.5", {"start": v(-144.64, -51.76) * mm, "end": v(-145.13, -47.16) * mm});
            skLineSegment(sketch, "E114.18.6", {"start": v(-140.96, -45.8) * mm, "end": v(-140.29, -47.87) * mm});
            skLineSegment(sketch, "E114.19.0", {"start": v(-139.4, -62.07) * mm, "end": v(-135.4, -60.28) * mm, "construction": true});
            skLineSegment(sketch, "E114.19.1", {"start": v(-136.29, -58.3) * mm, "end": v(-142.13, -58.32) * mm});
            skLineSegment(sketch, "E114.19.2", {"start": v(-142.13, -58.32) * mm, "end": v(-139.4, -62.07) * mm});
            skLineSegment(sketch, "E114.19.3", {"start": v(-135.4, -60.28) * mm, "end": v(-136.29, -58.3) * mm});
            skLineSegment(sketch, "E114.19.4", {"start": v(-134.52, -62.27) * mm, "end": v(-138.44, -66.6) * mm});
            skLineSegment(sketch, "E114.19.5", {"start": v(-138.44, -66.6) * mm, "end": v(-139.4, -62.07) * mm});
            skLineSegment(sketch, "E114.19.6", {"start": v(-135.4, -60.28) * mm, "end": v(-134.52, -62.27) * mm});
            skLineSegment(sketch, "E114.20.0", {"start": v(-132.15, -76.3) * mm, "end": v(-128.36, -74.1) * mm, "construction": true});
            skLineSegment(sketch, "E114.20.1", {"start": v(-129.44, -72.22) * mm, "end": v(-135.25, -72.85) * mm});
            skLineSegment(sketch, "E114.20.2", {"start": v(-135.25, -72.85) * mm, "end": v(-132.15, -76.3) * mm});
            skLineSegment(sketch, "E114.20.3", {"start": v(-128.36, -74.1) * mm, "end": v(-129.44, -72.22) * mm});
            skLineSegment(sketch, "E114.20.4", {"start": v(-127.27, -76) * mm, "end": v(-130.72, -80.7) * mm});
            skLineSegment(sketch, "E114.20.5", {"start": v(-130.72, -80.7) * mm, "end": v(-132.15, -76.3) * mm});
            skLineSegment(sketch, "E114.20.6", {"start": v(-128.36, -74.1) * mm, "end": v(-127.27, -76) * mm});
            skLineSegment(sketch, "E114.21.0", {"start": v(-123.45, -89.7) * mm, "end": v(-119.9, -87.12) * mm, "construction": true});
            skLineSegment(sketch, "E114.21.1", {"start": v(-121.19, -85.36) * mm, "end": v(-126.9, -86.6) * mm});
            skLineSegment(sketch, "E114.21.2", {"start": v(-126.9, -86.6) * mm, "end": v(-123.45, -89.7) * mm});
            skLineSegment(sketch, "E114.21.3", {"start": v(-119.9, -87.12) * mm, "end": v(-121.19, -85.36) * mm});
            skLineSegment(sketch, "E114.21.4", {"start": v(-118.63, -88.88) * mm, "end": v(-121.57, -93.93) * mm});
            skLineSegment(sketch, "E114.21.5", {"start": v(-121.57, -93.93) * mm, "end": v(-123.45, -89.7) * mm});
            skLineSegment(sketch, "E114.21.6", {"start": v(-119.9, -87.12) * mm, "end": v(-118.63, -88.88) * mm});
            skLineSegment(sketch, "E114.22.0", {"start": v(-113.4, -102.1) * mm, "end": v(-110.14, -99.17) * mm, "construction": true});
            skLineSegment(sketch, "E114.22.1", {"start": v(-111.6, -97.56) * mm, "end": v(-117.15, -99.38) * mm});
            skLineSegment(sketch, "E114.22.2", {"start": v(-117.15, -99.38) * mm, "end": v(-113.4, -102.1) * mm});
            skLineSegment(sketch, "E114.22.3", {"start": v(-110.14, -99.17) * mm, "end": v(-111.6, -97.56) * mm});
            skLineSegment(sketch, "E114.22.4", {"start": v(-108.7, -100.8) * mm, "end": v(-111.08, -106.12) * mm});
            skLineSegment(sketch, "E114.22.5", {"start": v(-111.08, -106.12) * mm, "end": v(-113.4, -102.1) * mm});
            skLineSegment(sketch, "E114.22.6", {"start": v(-110.14, -99.17) * mm, "end": v(-108.7, -100.8) * mm});
            skLineSegment(sketch, "E114.23.0", {"start": v(-102.1, -113.4) * mm, "end": v(-99.17, -110.14) * mm, "construction": true});
            skLineSegment(sketch, "E114.23.1", {"start": v(-100.8, -108.7) * mm, "end": v(-106.12, -111.08) * mm});
            skLineSegment(sketch, "E114.23.2", {"start": v(-106.12, -111.08) * mm, "end": v(-102.1, -113.4) * mm});
            skLineSegment(sketch, "E114.23.3", {"start": v(-99.17, -110.14) * mm, "end": v(-100.8, -108.7) * mm});
            skLineSegment(sketch, "E114.23.4", {"start": v(-97.56, -111.6) * mm, "end": v(-99.38, -117.15) * mm});
            skLineSegment(sketch, "E114.23.5", {"start": v(-99.38, -117.15) * mm, "end": v(-102.1, -113.4) * mm});
            skLineSegment(sketch, "E114.23.6", {"start": v(-99.17, -110.14) * mm, "end": v(-97.56, -111.6) * mm});
            skLineSegment(sketch, "E114.24.0", {"start": v(-89.7, -123.45) * mm, "end": v(-87.12, -119.9) * mm, "construction": true});
            skLineSegment(sketch, "E114.24.1", {"start": v(-88.88, -118.63) * mm, "end": v(-93.93, -121.57) * mm});
            skLineSegment(sketch, "E114.24.2", {"start": v(-93.93, -121.57) * mm, "end": v(-89.7, -123.45) * mm});
            skLineSegment(sketch, "E114.24.3", {"start": v(-87.12, -119.9) * mm, "end": v(-88.88, -118.63) * mm});
            skLineSegment(sketch, "E114.24.4", {"start": v(-85.36, -121.19) * mm, "end": v(-86.6, -126.9) * mm});
            skLineSegment(sketch, "E114.24.5", {"start": v(-86.6, -126.9) * mm, "end": v(-89.7, -123.45) * mm});
            skLineSegment(sketch, "E114.24.6", {"start": v(-87.12, -119.9) * mm, "end": v(-85.36, -121.19) * mm});
            skLineSegment(sketch, "E114.25.0", {"start": v(-76.3, -132.15) * mm, "end": v(-74.1, -128.36) * mm, "construction": true});
            skLineSegment(sketch, "E114.25.1", {"start": v(-76, -127.27) * mm, "end": v(-80.7, -130.72) * mm});
            skLineSegment(sketch, "E114.25.2", {"start": v(-80.7, -130.72) * mm, "end": v(-76.3, -132.15) * mm});
            skLineSegment(sketch, "E114.25.3", {"start": v(-74.1, -128.36) * mm, "end": v(-76, -127.27) * mm});
            skLineSegment(sketch, "E114.25.4", {"start": v(-72.22, -129.44) * mm, "end": v(-72.85, -135.25) * mm});
            skLineSegment(sketch, "E114.25.5", {"start": v(-72.85, -135.25) * mm, "end": v(-76.3, -132.15) * mm});
            skLineSegment(sketch, "E114.25.6", {"start": v(-74.1, -128.36) * mm, "end": v(-72.22, -129.44) * mm});
            skLineSegment(sketch, "E114.26.0", {"start": v(-62.07, -139.4) * mm, "end": v(-60.28, -135.4) * mm, "construction": true});
            skLineSegment(sketch, "E114.26.1", {"start": v(-62.27, -134.52) * mm, "end": v(-66.6, -138.44) * mm});
            skLineSegment(sketch, "E114.26.2", {"start": v(-66.6, -138.44) * mm, "end": v(-62.07, -139.4) * mm});
            skLineSegment(sketch, "E114.26.3", {"start": v(-60.28, -135.4) * mm, "end": v(-62.27, -134.52) * mm});
            skLineSegment(sketch, "E114.26.4", {"start": v(-58.3, -136.29) * mm, "end": v(-58.32, -142.13) * mm});
            skLineSegment(sketch, "E114.26.5", {"start": v(-58.32, -142.13) * mm, "end": v(-62.07, -139.4) * mm});
            skLineSegment(sketch, "E114.26.6", {"start": v(-60.28, -135.4) * mm, "end": v(-58.3, -136.29) * mm});
            skLineSegment(sketch, "E114.27.0", {"start": v(-47.16, -145.13) * mm, "end": v(-45.8, -140.96) * mm, "construction": true});
            skLineSegment(sketch, "E114.27.1", {"start": v(-47.87, -140.29) * mm, "end": v(-51.76, -144.64) * mm});
            skLineSegment(sketch, "E114.27.2", {"start": v(-51.76, -144.64) * mm, "end": v(-47.16, -145.13) * mm});
            skLineSegment(sketch, "E114.27.3", {"start": v(-45.8, -140.96) * mm, "end": v(-47.87, -140.29) * mm});
            skLineSegment(sketch, "E114.27.4", {"start": v(-43.73, -141.63) * mm, "end": v(-43.14, -147.44) * mm});
            skLineSegment(sketch, "E114.27.5", {"start": v(-43.14, -147.44) * mm, "end": v(-47.16, -145.13) * mm});
            skLineSegment(sketch, "E114.27.6", {"start": v(-45.8, -140.96) * mm, "end": v(-43.73, -141.63) * mm});
            skLineSegment(sketch, "E114.28.0", {"start": v(-31.73, -149.26) * mm, "end": v(-30.82, -144.98) * mm, "construction": true});
            skLineSegment(sketch, "E114.28.1", {"start": v(-32.94, -144.52) * mm, "end": v(-36.36, -149.26) * mm});
            skLineSegment(sketch, "E114.28.2", {"start": v(-36.36, -149.26) * mm, "end": v(-31.73, -149.26) * mm});
            skLineSegment(sketch, "E114.28.3", {"start": v(-30.82, -144.98) * mm, "end": v(-32.94, -144.52) * mm});
            skLineSegment(sketch, "E114.28.4", {"start": v(-28.69, -145.43) * mm, "end": v(-27.5, -151.14) * mm});
            skLineSegment(sketch, "E114.28.5", {"start": v(-27.5, -151.14) * mm, "end": v(-31.73, -149.26) * mm});
            skLineSegment(sketch, "E114.28.6", {"start": v(-30.82, -144.98) * mm, "end": v(-28.69, -145.43) * mm});
            skLineSegment(sketch, "E114.29.0", {"start": v(-15.95, -151.76) * mm, "end": v(-15.5, -147.4) * mm, "construction": true});
            skLineSegment(sketch, "E114.29.1", {"start": v(-17.65, -147.18) * mm, "end": v(-20.56, -152.24) * mm});
            skLineSegment(sketch, "E114.29.2", {"start": v(-20.56, -152.24) * mm, "end": v(-15.95, -151.76) * mm});
            skLineSegment(sketch, "E114.29.3", {"start": v(-15.5, -147.4) * mm, "end": v(-17.65, -147.18) * mm});
            skLineSegment(sketch, "E114.29.4", {"start": v(-13.33, -147.63) * mm, "end": v(-11.54, -153.2) * mm});
            skLineSegment(sketch, "E114.29.5", {"start": v(-11.54, -153.2) * mm, "end": v(-15.95, -151.76) * mm});
            skLineSegment(sketch, "E114.29.6", {"start": v(-15.5, -147.4) * mm, "end": v(-13.33, -147.63) * mm});
            skLineSegment(sketch, "E114.30.0", {"start": v(0, -152.6) * mm, "end": v(0, -148.21) * mm, "construction": true});
            skLineSegment(sketch, "E114.30.1", {"start": v(-2.17, -148.21) * mm, "end": v(-4.53, -153.56) * mm});
            skLineSegment(sketch, "E114.30.2", {"start": v(-4.53, -153.56) * mm, "end": v(0, -152.6) * mm});
            skLineSegment(sketch, "E114.30.3", {"start": v(0, -148.21) * mm, "end": v(-2.17, -148.21) * mm});
            skLineSegment(sketch, "E114.30.4", {"start": v(2.17, -148.21) * mm, "end": v(4.53, -153.56) * mm});
            skLineSegment(sketch, "E114.30.5", {"start": v(4.53, -153.56) * mm, "end": v(0, -152.6) * mm});
            skLineSegment(sketch, "E114.30.6", {"start": v(0, -148.21) * mm, "end": v(2.17, -148.21) * mm});
            skLineSegment(sketch, "E114.31.0", {"start": v(15.95, -151.76) * mm, "end": v(15.5, -147.4) * mm, "construction": true});
            skLineSegment(sketch, "E114.31.1", {"start": v(13.33, -147.63) * mm, "end": v(11.54, -153.2) * mm});
            skLineSegment(sketch, "E114.31.2", {"start": v(11.54, -153.2) * mm, "end": v(15.95, -151.76) * mm});
            skLineSegment(sketch, "E114.31.3", {"start": v(15.5, -147.4) * mm, "end": v(13.33, -147.63) * mm});
            skLineSegment(sketch, "E114.31.4", {"start": v(17.65, -147.18) * mm, "end": v(20.56, -152.24) * mm});
            skLineSegment(sketch, "E114.31.5", {"start": v(20.56, -152.24) * mm, "end": v(15.95, -151.76) * mm});
            skLineSegment(sketch, "E114.31.6", {"start": v(15.5, -147.4) * mm, "end": v(17.65, -147.18) * mm});
            skLineSegment(sketch, "E114.32.0", {"start": v(31.73, -149.26) * mm, "end": v(30.82, -144.98) * mm, "construction": true});
            skLineSegment(sketch, "E114.32.1", {"start": v(28.69, -145.43) * mm, "end": v(27.5, -151.14) * mm});
            skLineSegment(sketch, "E114.32.2", {"start": v(27.5, -151.14) * mm, "end": v(31.73, -149.26) * mm});
            skLineSegment(sketch, "E114.32.3", {"start": v(30.82, -144.98) * mm, "end": v(28.69, -145.43) * mm});
            skLineSegment(sketch, "E114.32.4", {"start": v(32.94, -144.52) * mm, "end": v(36.36, -149.26) * mm});
            skLineSegment(sketch, "E114.32.5", {"start": v(36.36, -149.26) * mm, "end": v(31.73, -149.26) * mm});
            skLineSegment(sketch, "E114.32.6", {"start": v(30.82, -144.98) * mm, "end": v(32.94, -144.52) * mm});
            skLineSegment(sketch, "E114.33.0", {"start": v(47.16, -145.13) * mm, "end": v(45.8, -140.96) * mm, "construction": true});
            skLineSegment(sketch, "E114.33.1", {"start": v(43.73, -141.63) * mm, "end": v(43.14, -147.44) * mm});
            skLineSegment(sketch, "E114.33.2", {"start": v(43.14, -147.44) * mm, "end": v(47.16, -145.13) * mm});
            skLineSegment(sketch, "E114.33.3", {"start": v(45.8, -140.96) * mm, "end": v(43.73, -141.63) * mm});
            skLineSegment(sketch, "E114.33.4", {"start": v(47.87, -140.29) * mm, "end": v(51.76, -144.64) * mm});
            skLineSegment(sketch, "E114.33.5", {"start": v(51.76, -144.64) * mm, "end": v(47.16, -145.13) * mm});
            skLineSegment(sketch, "E114.33.6", {"start": v(45.8, -140.96) * mm, "end": v(47.87, -140.29) * mm});
            skLineSegment(sketch, "E114.34.0", {"start": v(62.07, -139.4) * mm, "end": v(60.28, -135.4) * mm, "construction": true});
            skLineSegment(sketch, "E114.34.1", {"start": v(58.3, -136.29) * mm, "end": v(58.32, -142.13) * mm});
            skLineSegment(sketch, "E114.34.2", {"start": v(58.32, -142.13) * mm, "end": v(62.07, -139.4) * mm});
            skLineSegment(sketch, "E114.34.3", {"start": v(60.28, -135.4) * mm, "end": v(58.3, -136.29) * mm});
            skLineSegment(sketch, "E114.34.4", {"start": v(62.27, -134.52) * mm, "end": v(66.6, -138.44) * mm});
            skLineSegment(sketch, "E114.34.5", {"start": v(66.6, -138.44) * mm, "end": v(62.07, -139.4) * mm});
            skLineSegment(sketch, "E114.34.6", {"start": v(60.28, -135.4) * mm, "end": v(62.27, -134.52) * mm});
            skLineSegment(sketch, "E114.35.0", {"start": v(76.3, -132.15) * mm, "end": v(74.1, -128.36) * mm, "construction": true});
            skLineSegment(sketch, "E114.35.1", {"start": v(72.22, -129.44) * mm, "end": v(72.85, -135.25) * mm});
            skLineSegment(sketch, "E114.35.2", {"start": v(72.85, -135.25) * mm, "end": v(76.3, -132.15) * mm});
            skLineSegment(sketch, "E114.35.3", {"start": v(74.1, -128.36) * mm, "end": v(72.22, -129.44) * mm});
            skLineSegment(sketch, "E114.35.4", {"start": v(76, -127.27) * mm, "end": v(80.7, -130.72) * mm});
            skLineSegment(sketch, "E114.35.5", {"start": v(80.7, -130.72) * mm, "end": v(76.3, -132.15) * mm});
            skLineSegment(sketch, "E114.35.6", {"start": v(74.1, -128.36) * mm, "end": v(76, -127.27) * mm});
            skLineSegment(sketch, "E114.36.0", {"start": v(89.7, -123.45) * mm, "end": v(87.12, -119.9) * mm, "construction": true});
            skLineSegment(sketch, "E114.36.1", {"start": v(85.36, -121.19) * mm, "end": v(86.6, -126.9) * mm});
            skLineSegment(sketch, "E114.36.2", {"start": v(86.6, -126.9) * mm, "end": v(89.7, -123.45) * mm});
            skLineSegment(sketch, "E114.36.3", {"start": v(87.12, -119.9) * mm, "end": v(85.36, -121.19) * mm});
            skLineSegment(sketch, "E114.36.4", {"start": v(88.88, -118.63) * mm, "end": v(93.93, -121.57) * mm});
            skLineSegment(sketch, "E114.36.5", {"start": v(93.93, -121.57) * mm, "end": v(89.7, -123.45) * mm});
            skLineSegment(sketch, "E114.36.6", {"start": v(87.12, -119.9) * mm, "end": v(88.88, -118.63) * mm});
            skLineSegment(sketch, "E114.37.0", {"start": v(102.1, -113.4) * mm, "end": v(99.17, -110.14) * mm, "construction": true});
            skLineSegment(sketch, "E114.37.1", {"start": v(97.56, -111.6) * mm, "end": v(99.38, -117.15) * mm});
            skLineSegment(sketch, "E114.37.2", {"start": v(99.38, -117.15) * mm, "end": v(102.1, -113.4) * mm});
            skLineSegment(sketch, "E114.37.3", {"start": v(99.17, -110.14) * mm, "end": v(97.56, -111.6) * mm});
            skLineSegment(sketch, "E114.37.4", {"start": v(100.8, -108.7) * mm, "end": v(106.12, -111.08) * mm});
            skLineSegment(sketch, "E114.37.5", {"start": v(106.12, -111.08) * mm, "end": v(102.1, -113.4) * mm});
            skLineSegment(sketch, "E114.37.6", {"start": v(99.17, -110.14) * mm, "end": v(100.8, -108.7) * mm});
            skLineSegment(sketch, "E114.38.0", {"start": v(113.4, -102.1) * mm, "end": v(110.14, -99.17) * mm, "construction": true});
            skLineSegment(sketch, "E114.38.1", {"start": v(108.7, -100.8) * mm, "end": v(111.08, -106.12) * mm});
            skLineSegment(sketch, "E114.38.2", {"start": v(111.08, -106.12) * mm, "end": v(113.4, -102.1) * mm});
            skLineSegment(sketch, "E114.38.3", {"start": v(110.14, -99.17) * mm, "end": v(108.7, -100.8) * mm});
            skLineSegment(sketch, "E114.38.4", {"start": v(111.6, -97.56) * mm, "end": v(117.15, -99.38) * mm});
            skLineSegment(sketch, "E114.38.5", {"start": v(117.15, -99.38) * mm, "end": v(113.4, -102.1) * mm});
            skLineSegment(sketch, "E114.38.6", {"start": v(110.14, -99.17) * mm, "end": v(111.6, -97.56) * mm});
            skLineSegment(sketch, "E114.39.0", {"start": v(123.45, -89.7) * mm, "end": v(119.9, -87.12) * mm, "construction": true});
            skLineSegment(sketch, "E114.39.1", {"start": v(118.63, -88.88) * mm, "end": v(121.57, -93.93) * mm});
            skLineSegment(sketch, "E114.39.2", {"start": v(121.57, -93.93) * mm, "end": v(123.45, -89.7) * mm});
            skLineSegment(sketch, "E114.39.3", {"start": v(119.9, -87.12) * mm, "end": v(118.63, -88.88) * mm});
            skLineSegment(sketch, "E114.39.4", {"start": v(121.19, -85.36) * mm, "end": v(126.9, -86.6) * mm});
            skLineSegment(sketch, "E114.39.5", {"start": v(126.9, -86.6) * mm, "end": v(123.45, -89.7) * mm});
            skLineSegment(sketch, "E114.39.6", {"start": v(119.9, -87.12) * mm, "end": v(121.19, -85.36) * mm});
            skLineSegment(sketch, "E114.40.0", {"start": v(132.15, -76.3) * mm, "end": v(128.36, -74.1) * mm, "construction": true});
            skLineSegment(sketch, "E114.40.1", {"start": v(127.27, -76) * mm, "end": v(130.72, -80.7) * mm});
            skLineSegment(sketch, "E114.40.2", {"start": v(130.72, -80.7) * mm, "end": v(132.15, -76.3) * mm});
            skLineSegment(sketch, "E114.40.3", {"start": v(128.36, -74.1) * mm, "end": v(127.27, -76) * mm});
            skLineSegment(sketch, "E114.40.4", {"start": v(129.44, -72.22) * mm, "end": v(135.25, -72.85) * mm});
            skLineSegment(sketch, "E114.40.5", {"start": v(135.25, -72.85) * mm, "end": v(132.15, -76.3) * mm});
            skLineSegment(sketch, "E114.40.6", {"start": v(128.36, -74.1) * mm, "end": v(129.44, -72.22) * mm});
            skLineSegment(sketch, "E114.41.0", {"start": v(139.4, -62.07) * mm, "end": v(135.4, -60.28) * mm, "construction": true});
            skLineSegment(sketch, "E114.41.1", {"start": v(134.52, -62.27) * mm, "end": v(138.44, -66.6) * mm});
            skLineSegment(sketch, "E114.41.2", {"start": v(138.44, -66.6) * mm, "end": v(139.4, -62.07) * mm});
            skLineSegment(sketch, "E114.41.3", {"start": v(135.4, -60.28) * mm, "end": v(134.52, -62.27) * mm});
            skLineSegment(sketch, "E114.41.4", {"start": v(136.29, -58.3) * mm, "end": v(142.13, -58.32) * mm});
            skLineSegment(sketch, "E114.41.5", {"start": v(142.13, -58.32) * mm, "end": v(139.4, -62.07) * mm});
            skLineSegment(sketch, "E114.41.6", {"start": v(135.4, -60.28) * mm, "end": v(136.29, -58.3) * mm});
            skLineSegment(sketch, "E114.42.0", {"start": v(145.13, -47.16) * mm, "end": v(140.96, -45.8) * mm, "construction": true});
            skLineSegment(sketch, "E114.42.1", {"start": v(140.29, -47.87) * mm, "end": v(144.64, -51.76) * mm});
            skLineSegment(sketch, "E114.42.2", {"start": v(144.64, -51.76) * mm, "end": v(145.13, -47.16) * mm});
            skLineSegment(sketch, "E114.42.3", {"start": v(140.96, -45.8) * mm, "end": v(140.29, -47.87) * mm});
            skLineSegment(sketch, "E114.42.4", {"start": v(141.63, -43.73) * mm, "end": v(147.44, -43.14) * mm});
            skLineSegment(sketch, "E114.42.5", {"start": v(147.44, -43.14) * mm, "end": v(145.13, -47.16) * mm});
            skLineSegment(sketch, "E114.42.6", {"start": v(140.96, -45.8) * mm, "end": v(141.63, -43.73) * mm});
            skLineSegment(sketch, "E114.43.0", {"start": v(149.26, -31.73) * mm, "end": v(144.98, -30.82) * mm, "construction": true});
            skLineSegment(sketch, "E114.43.1", {"start": v(144.52, -32.94) * mm, "end": v(149.26, -36.36) * mm});
            skLineSegment(sketch, "E114.43.2", {"start": v(149.26, -36.36) * mm, "end": v(149.26, -31.73) * mm});
            skLineSegment(sketch, "E114.43.3", {"start": v(144.98, -30.82) * mm, "end": v(144.52, -32.94) * mm});
            skLineSegment(sketch, "E114.43.4", {"start": v(145.43, -28.69) * mm, "end": v(151.14, -27.5) * mm});
            skLineSegment(sketch, "E114.43.5", {"start": v(151.14, -27.5) * mm, "end": v(149.26, -31.73) * mm});
            skLineSegment(sketch, "E114.43.6", {"start": v(144.98, -30.82) * mm, "end": v(145.43, -28.69) * mm});
            skLineSegment(sketch, "E114.44.0", {"start": v(151.76, -15.95) * mm, "end": v(147.4, -15.5) * mm, "construction": true});
            skLineSegment(sketch, "E114.44.1", {"start": v(147.18, -17.65) * mm, "end": v(152.24, -20.56) * mm});
            skLineSegment(sketch, "E114.44.2", {"start": v(152.24, -20.56) * mm, "end": v(151.76, -15.95) * mm});
            skLineSegment(sketch, "E114.44.3", {"start": v(147.4, -15.5) * mm, "end": v(147.18, -17.65) * mm});
            skLineSegment(sketch, "E114.44.4", {"start": v(147.63, -13.33) * mm, "end": v(153.2, -11.54) * mm});
            skLineSegment(sketch, "E114.44.5", {"start": v(153.2, -11.54) * mm, "end": v(151.76, -15.95) * mm});
            skLineSegment(sketch, "E114.44.6", {"start": v(147.4, -15.5) * mm, "end": v(147.63, -13.33) * mm});
            skLineSegment(sketch, "E114.45.0", {"start": v(152.6, 0) * mm, "end": v(148.21, 0) * mm, "construction": true});
            skLineSegment(sketch, "E114.45.1", {"start": v(148.21, -2.17) * mm, "end": v(153.56, -4.53) * mm});
            skLineSegment(sketch, "E114.45.2", {"start": v(153.56, -4.53) * mm, "end": v(152.6, 0) * mm});
            skLineSegment(sketch, "E114.45.3", {"start": v(148.21, 0) * mm, "end": v(148.21, -2.17) * mm});
            skLineSegment(sketch, "E114.45.4", {"start": v(148.21, 2.17) * mm, "end": v(153.56, 4.53) * mm});
            skLineSegment(sketch, "E114.45.5", {"start": v(153.56, 4.53) * mm, "end": v(152.6, 0) * mm});
            skLineSegment(sketch, "E114.45.6", {"start": v(148.21, 0) * mm, "end": v(148.21, 2.17) * mm});
            skLineSegment(sketch, "E114.46.0", {"start": v(151.76, 15.95) * mm, "end": v(147.4, 15.5) * mm, "construction": true});
            skLineSegment(sketch, "E114.46.1", {"start": v(147.63, 13.33) * mm, "end": v(153.2, 11.54) * mm});
            skLineSegment(sketch, "E114.46.2", {"start": v(153.2, 11.54) * mm, "end": v(151.76, 15.95) * mm});
            skLineSegment(sketch, "E114.46.3", {"start": v(147.4, 15.5) * mm, "end": v(147.63, 13.33) * mm});
            skLineSegment(sketch, "E114.46.4", {"start": v(147.18, 17.65) * mm, "end": v(152.24, 20.56) * mm});
            skLineSegment(sketch, "E114.46.5", {"start": v(152.24, 20.56) * mm, "end": v(151.76, 15.95) * mm});
            skLineSegment(sketch, "E114.46.6", {"start": v(147.4, 15.5) * mm, "end": v(147.18, 17.65) * mm});
            skLineSegment(sketch, "E114.47.0", {"start": v(149.26, 31.73) * mm, "end": v(144.98, 30.82) * mm, "construction": true});
            skLineSegment(sketch, "E114.47.1", {"start": v(145.43, 28.69) * mm, "end": v(151.14, 27.5) * mm});
            skLineSegment(sketch, "E114.47.2", {"start": v(151.14, 27.5) * mm, "end": v(149.26, 31.73) * mm});
            skLineSegment(sketch, "E114.47.3", {"start": v(144.98, 30.82) * mm, "end": v(145.43, 28.69) * mm});
            skLineSegment(sketch, "E114.47.4", {"start": v(144.52, 32.94) * mm, "end": v(149.26, 36.36) * mm});
            skLineSegment(sketch, "E114.47.5", {"start": v(149.26, 36.36) * mm, "end": v(149.26, 31.73) * mm});
            skLineSegment(sketch, "E114.47.6", {"start": v(144.98, 30.82) * mm, "end": v(144.52, 32.94) * mm});
            skLineSegment(sketch, "E114.48.0", {"start": v(145.13, 47.16) * mm, "end": v(140.96, 45.8) * mm, "construction": true});
            skLineSegment(sketch, "E114.48.1", {"start": v(141.63, 43.73) * mm, "end": v(147.44, 43.14) * mm});
            skLineSegment(sketch, "E114.48.2", {"start": v(147.44, 43.14) * mm, "end": v(145.13, 47.16) * mm});
            skLineSegment(sketch, "E114.48.3", {"start": v(140.96, 45.8) * mm, "end": v(141.63, 43.73) * mm});
            skLineSegment(sketch, "E114.48.4", {"start": v(140.29, 47.87) * mm, "end": v(144.64, 51.76) * mm});
            skLineSegment(sketch, "E114.48.5", {"start": v(144.64, 51.76) * mm, "end": v(145.13, 47.16) * mm});
            skLineSegment(sketch, "E114.48.6", {"start": v(140.96, 45.8) * mm, "end": v(140.29, 47.87) * mm});
            skLineSegment(sketch, "E114.49.0", {"start": v(139.4, 62.07) * mm, "end": v(135.4, 60.28) * mm, "construction": true});
            skLineSegment(sketch, "E114.49.1", {"start": v(136.29, 58.3) * mm, "end": v(142.13, 58.32) * mm});
            skLineSegment(sketch, "E114.49.2", {"start": v(142.13, 58.32) * mm, "end": v(139.4, 62.07) * mm});
            skLineSegment(sketch, "E114.49.3", {"start": v(135.4, 60.28) * mm, "end": v(136.29, 58.3) * mm});
            skLineSegment(sketch, "E114.49.4", {"start": v(134.52, 62.27) * mm, "end": v(138.44, 66.6) * mm});
            skLineSegment(sketch, "E114.49.5", {"start": v(138.44, 66.6) * mm, "end": v(139.4, 62.07) * mm});
            skLineSegment(sketch, "E114.49.6", {"start": v(135.4, 60.28) * mm, "end": v(134.52, 62.27) * mm});
            skLineSegment(sketch, "E114.50.0", {"start": v(132.15, 76.3) * mm, "end": v(128.36, 74.1) * mm, "construction": true});
            skLineSegment(sketch, "E114.50.1", {"start": v(129.44, 72.22) * mm, "end": v(135.25, 72.85) * mm});
            skLineSegment(sketch, "E114.50.2", {"start": v(135.25, 72.85) * mm, "end": v(132.15, 76.3) * mm});
            skLineSegment(sketch, "E114.50.3", {"start": v(128.36, 74.1) * mm, "end": v(129.44, 72.22) * mm});
            skLineSegment(sketch, "E114.50.4", {"start": v(127.27, 76) * mm, "end": v(130.72, 80.7) * mm});
            skLineSegment(sketch, "E114.50.5", {"start": v(130.72, 80.7) * mm, "end": v(132.15, 76.3) * mm});
            skLineSegment(sketch, "E114.50.6", {"start": v(128.36, 74.1) * mm, "end": v(127.27, 76) * mm});
            skLineSegment(sketch, "E114.51.0", {"start": v(123.45, 89.7) * mm, "end": v(119.9, 87.12) * mm, "construction": true});
            skLineSegment(sketch, "E114.51.1", {"start": v(121.19, 85.36) * mm, "end": v(126.9, 86.6) * mm});
            skLineSegment(sketch, "E114.51.2", {"start": v(126.9, 86.6) * mm, "end": v(123.45, 89.7) * mm});
            skLineSegment(sketch, "E114.51.3", {"start": v(119.9, 87.12) * mm, "end": v(121.19, 85.36) * mm});
            skLineSegment(sketch, "E114.51.4", {"start": v(118.63, 88.88) * mm, "end": v(121.57, 93.93) * mm});
            skLineSegment(sketch, "E114.51.5", {"start": v(121.57, 93.93) * mm, "end": v(123.45, 89.7) * mm});
            skLineSegment(sketch, "E114.51.6", {"start": v(119.9, 87.12) * mm, "end": v(118.63, 88.88) * mm});
            skLineSegment(sketch, "E114.52.0", {"start": v(113.4, 102.1) * mm, "end": v(110.14, 99.17) * mm, "construction": true});
            skLineSegment(sketch, "E114.52.1", {"start": v(111.6, 97.56) * mm, "end": v(117.15, 99.38) * mm});
            skLineSegment(sketch, "E114.52.2", {"start": v(117.15, 99.38) * mm, "end": v(113.4, 102.1) * mm});
            skLineSegment(sketch, "E114.52.3", {"start": v(110.14, 99.17) * mm, "end": v(111.6, 97.56) * mm});
            skLineSegment(sketch, "E114.52.4", {"start": v(108.7, 100.8) * mm, "end": v(111.08, 106.12) * mm});
            skLineSegment(sketch, "E114.52.5", {"start": v(111.08, 106.12) * mm, "end": v(113.4, 102.1) * mm});
            skLineSegment(sketch, "E114.52.6", {"start": v(110.14, 99.17) * mm, "end": v(108.7, 100.8) * mm});
            skLineSegment(sketch, "E114.53.0", {"start": v(102.1, 113.4) * mm, "end": v(99.17, 110.14) * mm, "construction": true});
            skLineSegment(sketch, "E114.53.1", {"start": v(100.8, 108.7) * mm, "end": v(106.12, 111.08) * mm});
            skLineSegment(sketch, "E114.53.2", {"start": v(106.12, 111.08) * mm, "end": v(102.1, 113.4) * mm});
            skLineSegment(sketch, "E114.53.3", {"start": v(99.17, 110.14) * mm, "end": v(100.8, 108.7) * mm});
            skLineSegment(sketch, "E114.53.4", {"start": v(97.56, 111.6) * mm, "end": v(99.38, 117.15) * mm});
            skLineSegment(sketch, "E114.53.5", {"start": v(99.38, 117.15) * mm, "end": v(102.1, 113.4) * mm});
            skLineSegment(sketch, "E114.53.6", {"start": v(99.17, 110.14) * mm, "end": v(97.56, 111.6) * mm});
            skLineSegment(sketch, "E114.54.0", {"start": v(89.7, 123.45) * mm, "end": v(87.12, 119.9) * mm, "construction": true});
            skLineSegment(sketch, "E114.54.1", {"start": v(88.88, 118.63) * mm, "end": v(93.93, 121.57) * mm});
            skLineSegment(sketch, "E114.54.2", {"start": v(93.93, 121.57) * mm, "end": v(89.7, 123.45) * mm});
            skLineSegment(sketch, "E114.54.3", {"start": v(87.12, 119.9) * mm, "end": v(88.88, 118.63) * mm});
            skLineSegment(sketch, "E114.54.4", {"start": v(85.36, 121.19) * mm, "end": v(86.6, 126.9) * mm});
            skLineSegment(sketch, "E114.54.5", {"start": v(86.6, 126.9) * mm, "end": v(89.7, 123.45) * mm});
            skLineSegment(sketch, "E114.54.6", {"start": v(87.12, 119.9) * mm, "end": v(85.36, 121.19) * mm});
            skLineSegment(sketch, "E114.55.0", {"start": v(76.3, 132.15) * mm, "end": v(74.1, 128.36) * mm, "construction": true});
            skLineSegment(sketch, "E114.55.1", {"start": v(76, 127.27) * mm, "end": v(80.7, 130.72) * mm});
            skLineSegment(sketch, "E114.55.2", {"start": v(80.7, 130.72) * mm, "end": v(76.3, 132.15) * mm});
            skLineSegment(sketch, "E114.55.3", {"start": v(74.1, 128.36) * mm, "end": v(76, 127.27) * mm});
            skLineSegment(sketch, "E114.55.4", {"start": v(72.22, 129.44) * mm, "end": v(72.85, 135.25) * mm});
            skLineSegment(sketch, "E114.55.5", {"start": v(72.85, 135.25) * mm, "end": v(76.3, 132.15) * mm});
            skLineSegment(sketch, "E114.55.6", {"start": v(74.1, 128.36) * mm, "end": v(72.22, 129.44) * mm});
            skLineSegment(sketch, "E114.56.0", {"start": v(62.07, 139.4) * mm, "end": v(60.28, 135.4) * mm, "construction": true});
            skLineSegment(sketch, "E114.56.1", {"start": v(62.27, 134.52) * mm, "end": v(66.6, 138.44) * mm});
            skLineSegment(sketch, "E114.56.2", {"start": v(66.6, 138.44) * mm, "end": v(62.07, 139.4) * mm});
            skLineSegment(sketch, "E114.56.3", {"start": v(60.28, 135.4) * mm, "end": v(62.27, 134.52) * mm});
            skLineSegment(sketch, "E114.56.4", {"start": v(58.3, 136.29) * mm, "end": v(58.32, 142.13) * mm});
            skLineSegment(sketch, "E114.56.5", {"start": v(58.32, 142.13) * mm, "end": v(62.07, 139.4) * mm});
            skLineSegment(sketch, "E114.56.6", {"start": v(60.28, 135.4) * mm, "end": v(58.3, 136.29) * mm});
            skLineSegment(sketch, "E114.57.0", {"start": v(47.16, 145.13) * mm, "end": v(45.8, 140.96) * mm, "construction": true});
            skLineSegment(sketch, "E114.57.1", {"start": v(47.87, 140.29) * mm, "end": v(51.76, 144.64) * mm});
            skLineSegment(sketch, "E114.57.2", {"start": v(51.76, 144.64) * mm, "end": v(47.16, 145.13) * mm});
            skLineSegment(sketch, "E114.57.3", {"start": v(45.8, 140.96) * mm, "end": v(47.87, 140.29) * mm});
            skLineSegment(sketch, "E114.57.4", {"start": v(43.73, 141.63) * mm, "end": v(43.14, 147.44) * mm});
            skLineSegment(sketch, "E114.57.5", {"start": v(43.14, 147.44) * mm, "end": v(47.16, 145.13) * mm});
            skLineSegment(sketch, "E114.57.6", {"start": v(45.8, 140.96) * mm, "end": v(43.73, 141.63) * mm});
            skLineSegment(sketch, "E114.58.0", {"start": v(31.73, 149.26) * mm, "end": v(30.82, 144.98) * mm, "construction": true});
            skLineSegment(sketch, "E114.58.1", {"start": v(32.94, 144.52) * mm, "end": v(36.36, 149.26) * mm});
            skLineSegment(sketch, "E114.58.2", {"start": v(36.36, 149.26) * mm, "end": v(31.73, 149.26) * mm});
            skLineSegment(sketch, "E114.58.3", {"start": v(30.82, 144.98) * mm, "end": v(32.94, 144.52) * mm});
            skLineSegment(sketch, "E114.58.4", {"start": v(28.69, 145.43) * mm, "end": v(27.5, 151.14) * mm});
            skLineSegment(sketch, "E114.58.5", {"start": v(27.5, 151.14) * mm, "end": v(31.73, 149.26) * mm});
            skLineSegment(sketch, "E114.58.6", {"start": v(30.82, 144.98) * mm, "end": v(28.69, 145.43) * mm});
            skLineSegment(sketch, "E114.59.0", {"start": v(15.95, 151.76) * mm, "end": v(15.5, 147.4) * mm, "construction": true});
            skLineSegment(sketch, "E114.59.1", {"start": v(17.65, 147.18) * mm, "end": v(20.56, 152.24) * mm});
            skLineSegment(sketch, "E114.59.2", {"start": v(20.56, 152.24) * mm, "end": v(15.95, 151.76) * mm});
            skLineSegment(sketch, "E114.59.3", {"start": v(15.5, 147.4) * mm, "end": v(17.65, 147.18) * mm});
            skLineSegment(sketch, "E114.59.4", {"start": v(13.33, 147.63) * mm, "end": v(11.54, 153.2) * mm});
            skLineSegment(sketch, "E114.59.5", {"start": v(11.54, 153.2) * mm, "end": v(15.95, 151.76) * mm});
            skLineSegment(sketch, "E114.59.6", {"start": v(15.5, 147.4) * mm, "end": v(13.33, 147.63) * mm});
            skPoint(sketch, "E114.center", {"position": v(0, 0) * mm});
            skSolve(sketch);
        }
        {
            var Q0;
            Q0 = qSketchRegion(id + "F13", true);
            extrude(context, id + "F14", {"entities" : qUnion([Q0]), "operationType" : NewBodyOperationType.REMOVE, "endBound" : BoundingType.THROUGH_ALL, "oppositeDirection" : true, "depth" : 25.4 * mm, "hasSecondDirection" : true, "secondDirectionBound" : SecondDirectionBoundingType.THROUGH_ALL, "secondDirectionOppositeDirection" : false, "secondDirectionDepth" : 25.4 * mm});
        }
        {
            var Q0;
            Q0=qCreatedBy(makeId("Front.planeOp"),FACE);
            var sketch = newSketch(context, id + "F15", { "sketchPlane" : qUnion([Q0])});
            skLineSegment(sketch, "E115", {"start": v(59.41, 17.53) * mm, "end": v(58.88, 16.6) * mm});
            skLineSegment(sketch, "E116", {"start": v(58.88, 16.6) * mm, "end": v(58.35, 17.53) * mm});
            skLineSegment(sketch, "E117", {"start": v(58.35, 17.53) * mm, "end": v(59.41, 17.53) * mm});
            skLineSegment(sketch, "E118", {"start": v(97.08, 0) * mm, "end": v(-97.08, 0) * mm, "construction": true});
            skLineSegment(sketch, "E119", {"start": v(58.88, 16.6) * mm, "end": v(58.88, 17.53) * mm, "construction": true});
            skLineSegment(sketch, "E120.0", {"start": v(59.41, -17.46) * mm, "end": v(59.41, 17.46) * mm, "construction": true});
            skLineSegment(sketch, "E121.1.0.0", {"start": v(57.04, 17.53) * mm, "end": v(58.1, 17.53) * mm});
            skLineSegment(sketch, "E121.1.0.1", {"start": v(58.1, 17.53) * mm, "end": v(57.57, 16.6) * mm});
            skLineSegment(sketch, "E121.1.0.2", {"start": v(57.57, 16.6) * mm, "end": v(57.04, 17.53) * mm});
            skLineSegment(sketch, "E121.2.0.0", {"start": v(55.73, 17.53) * mm, "end": v(56.79, 17.53) * mm});
            skLineSegment(sketch, "E121.2.0.1", {"start": v(56.79, 17.53) * mm, "end": v(56.26, 16.6) * mm});
            skLineSegment(sketch, "E121.2.0.2", {"start": v(56.26, 16.6) * mm, "end": v(55.73, 17.53) * mm});
            skLineSegment(sketch, "E121.direction1", {"start": v(58.35, 17.53) * mm, "end": v(57.04, 17.53) * mm, "construction": true});
            skLineSegment(sketch, "E122.0.3.0", {"start": v(54.42, 17.53) * mm, "end": v(55.48, 17.53) * mm});
            skLineSegment(sketch, "E122.3.3.0", {"start": v(55.48, 17.53) * mm, "end": v(54.95, 16.6) * mm});
            skLineSegment(sketch, "E122.6.3.0", {"start": v(54.95, 16.6) * mm, "end": v(54.42, 17.53) * mm});
            skLineSegment(sketch, "E122.0.4.0", {"start": v(53.1, 17.53) * mm, "end": v(54.16, 17.53) * mm});
            skLineSegment(sketch, "E122.3.4.0", {"start": v(54.16, 17.53) * mm, "end": v(53.63, 16.6) * mm});
            skLineSegment(sketch, "E122.6.4.0", {"start": v(53.63, 16.6) * mm, "end": v(53.1, 17.53) * mm});
            skLineSegment(sketch, "E122.0.5.0", {"start": v(51.8, 17.53) * mm, "end": v(52.85, 17.53) * mm});
            skLineSegment(sketch, "E122.3.5.0", {"start": v(52.85, 17.53) * mm, "end": v(52.32, 16.6) * mm});
            skLineSegment(sketch, "E122.6.5.0", {"start": v(52.32, 16.6) * mm, "end": v(51.8, 17.53) * mm});
            skLineSegment(sketch, "E122.0.6.0", {"start": v(50.48, 17.53) * mm, "end": v(51.54, 17.53) * mm});
            skLineSegment(sketch, "E122.3.6.0", {"start": v(51.54, 17.53) * mm, "end": v(51, 16.6) * mm});
            skLineSegment(sketch, "E122.6.6.0", {"start": v(51, 16.6) * mm, "end": v(50.48, 17.53) * mm});
            skLineSegment(sketch, "E122.0.7.0", {"start": v(49.17, 17.53) * mm, "end": v(50.23, 17.53) * mm});
            skLineSegment(sketch, "E122.3.7.0", {"start": v(50.23, 17.53) * mm, "end": v(49.7, 16.6) * mm});
            skLineSegment(sketch, "E122.6.7.0", {"start": v(49.7, 16.6) * mm, "end": v(49.17, 17.53) * mm});
            skLineSegment(sketch, "E123.0.8.0", {"start": v(47.86, 17.53) * mm, "end": v(48.91, 17.53) * mm});
            skLineSegment(sketch, "E123.3.8.0", {"start": v(48.91, 17.53) * mm, "end": v(48.38, 16.6) * mm});
            skLineSegment(sketch, "E123.6.8.0", {"start": v(48.38, 16.6) * mm, "end": v(47.86, 17.53) * mm});
            skLineSegment(sketch, "E123.0.9.0", {"start": v(46.54, 17.53) * mm, "end": v(47.6, 17.53) * mm});
            skLineSegment(sketch, "E123.3.9.0", {"start": v(47.6, 17.53) * mm, "end": v(47.07, 16.6) * mm});
            skLineSegment(sketch, "E123.6.9.0", {"start": v(47.07, 16.6) * mm, "end": v(46.54, 17.53) * mm});
            skLineSegment(sketch, "E124", {"start": v(0, 0) * mm, "end": v(0, -373.04) * mm});
            skLineSegment(sketch, "E125.MirrorCS", {"start": v(-58.35, 17.53) * mm, "end": v(-57.04, 17.53) * mm});
            skLineSegment(sketch, "E126.MirrorCS", {"start": v(-58.88, 16.6) * mm, "end": v(-58.35, 17.53) * mm});
            skLineSegment(sketch, "E127.MirrorCS", {"start": v(-59.41, 17.53) * mm, "end": v(-58.88, 16.6) * mm});
            skLineSegment(sketch, "E128.MirrorCS", {"start": v(-57.04, 17.53) * mm, "end": v(-58.1, 17.53) * mm});
            skLineSegment(sketch, "E129.MirrorCS", {"start": v(-58.88, 16.6) * mm, "end": v(-58.88, 17.53) * mm});
            skLineSegment(sketch, "E130.MirrorCS", {"start": v(-58.35, 17.53) * mm, "end": v(-59.41, 17.53) * mm});
            skLineSegment(sketch, "E131.MirrorCS", {"start": v(-54.42, 17.53) * mm, "end": v(-55.48, 17.53) * mm});
            skLineSegment(sketch, "E132.MirrorCS", {"start": v(-55.73, 17.53) * mm, "end": v(-56.79, 17.53) * mm});
            skLineSegment(sketch, "E133.MirrorCS", {"start": v(-54.95, 16.6) * mm, "end": v(-54.42, 17.53) * mm});
            skLineSegment(sketch, "E134.MirrorCS", {"start": v(-55.48, 17.53) * mm, "end": v(-54.95, 16.6) * mm});
            skLineSegment(sketch, "E135.MirrorCS", {"start": v(-53.1, 17.53) * mm, "end": v(-54.16, 17.53) * mm});
            skLineSegment(sketch, "E136.MirrorCS", {"start": v(-51.8, 17.53) * mm, "end": v(-52.85, 17.53) * mm});
            skLineSegment(sketch, "E137.MirrorCS", {"start": v(-56.26, 16.6) * mm, "end": v(-55.73, 17.53) * mm});
            skLineSegment(sketch, "E138.MirrorCS", {"start": v(-56.79, 17.53) * mm, "end": v(-56.26, 16.6) * mm});
            skLineSegment(sketch, "E139.MirrorCS", {"start": v(-57.57, 16.6) * mm, "end": v(-57.04, 17.53) * mm});
            skLineSegment(sketch, "E140.MirrorCS", {"start": v(-58.1, 17.53) * mm, "end": v(-57.57, 16.6) * mm});
            skLineSegment(sketch, "E141.MirrorCS", {"start": v(-53.63, 16.6) * mm, "end": v(-53.1, 17.53) * mm});
            skLineSegment(sketch, "E142.MirrorCS", {"start": v(-54.16, 17.53) * mm, "end": v(-53.63, 16.6) * mm});
            skLineSegment(sketch, "E143.MirrorCS", {"start": v(-52.85, 17.53) * mm, "end": v(-52.32, 16.6) * mm});
            skLineSegment(sketch, "E144.MirrorCS", {"start": v(-52.32, 16.6) * mm, "end": v(-51.8, 17.53) * mm});
            skLineSegment(sketch, "E145.MirrorCS", {"start": v(-50.48, 17.53) * mm, "end": v(-51.54, 17.53) * mm});
            skLineSegment(sketch, "E146.MirrorCS", {"start": v(-46.54, 17.53) * mm, "end": v(-47.6, 17.53) * mm});
            skLineSegment(sketch, "E147.MirrorCS", {"start": v(-59.41, -17.46) * mm, "end": v(-59.41, 17.46) * mm});
            skLineSegment(sketch, "E148.MirrorCS", {"start": v(-49.7, 16.6) * mm, "end": v(-49.17, 17.53) * mm});
            skLineSegment(sketch, "E149.MirrorCS", {"start": v(-47.6, 17.53) * mm, "end": v(-47.07, 16.6) * mm});
            skLineSegment(sketch, "E150.MirrorCS", {"start": v(-51.54, 17.53) * mm, "end": v(-51, 16.6) * mm});
            skLineSegment(sketch, "E151.MirrorCS", {"start": v(-48.38, 16.6) * mm, "end": v(-47.86, 17.53) * mm});
            skLineSegment(sketch, "E152.MirrorCS", {"start": v(-48.91, 17.53) * mm, "end": v(-48.38, 16.6) * mm});
            skLineSegment(sketch, "E153.MirrorCS", {"start": v(-50.23, 17.53) * mm, "end": v(-49.7, 16.6) * mm});
            skLineSegment(sketch, "E154.MirrorCS", {"start": v(-49.17, 17.53) * mm, "end": v(-50.23, 17.53) * mm});
            skLineSegment(sketch, "E155.MirrorCS", {"start": v(-51, 16.6) * mm, "end": v(-50.48, 17.53) * mm});
            skLineSegment(sketch, "E156.MirrorCS", {"start": v(-47.86, 17.53) * mm, "end": v(-48.91, 17.53) * mm});
            skLineSegment(sketch, "E157.MirrorCS", {"start": v(-47.07, 16.6) * mm, "end": v(-46.54, 17.53) * mm});
            skLineSegment(sketch, "E158", {"start": v(97.08, 5.08) * mm, "end": v(96.63, 4.3) * mm});
            skLineSegment(sketch, "E159", {"start": v(96.63, 4.3) * mm, "end": v(96.18, 5.08) * mm});
            skLineSegment(sketch, "E160", {"start": v(96.18, 5.08) * mm, "end": v(97.08, 5.08) * mm});
            skLineSegment(sketch, "E161", {"start": v(96.63, 5.08) * mm, "end": v(96.63, 4.3) * mm, "construction": true});
            skLineSegment(sketch, "E162.1.0.0", {"start": v(95.63, 4.3) * mm, "end": v(95.18, 5.08) * mm});
            skLineSegment(sketch, "E162.1.0.1", {"start": v(95.18, 5.08) * mm, "end": v(96.08, 5.08) * mm});
            skLineSegment(sketch, "E162.1.0.2", {"start": v(95.63, 5.08) * mm, "end": v(95.63, 4.3) * mm, "construction": true});
            skLineSegment(sketch, "E162.1.0.3", {"start": v(96.08, 5.08) * mm, "end": v(95.63, 4.3) * mm});
            skLineSegment(sketch, "E162.2.0.0", {"start": v(94.63, 4.3) * mm, "end": v(94.18, 5.08) * mm});
            skLineSegment(sketch, "E162.2.0.1", {"start": v(94.18, 5.08) * mm, "end": v(95.08, 5.08) * mm});
            skLineSegment(sketch, "E162.2.0.2", {"start": v(94.63, 5.08) * mm, "end": v(94.63, 4.3) * mm, "construction": true});
            skLineSegment(sketch, "E162.2.0.3", {"start": v(95.08, 5.08) * mm, "end": v(94.63, 4.3) * mm});
            skLineSegment(sketch, "E162.direction1", {"start": v(96.63, 4.3) * mm, "end": v(95.63, 4.3) * mm, "construction": true});
            skLineSegment(sketch, "E163.0.3.0", {"start": v(93.63, 4.3) * mm, "end": v(93.18, 5.08) * mm});
            skLineSegment(sketch, "E163.3.3.0", {"start": v(93.18, 5.08) * mm, "end": v(94.08, 5.08) * mm});
            skLineSegment(sketch, "E163.6.3.0", {"start": v(93.63, 5.08) * mm, "end": v(93.63, 4.3) * mm, "construction": true});
            skLineSegment(sketch, "E163.9.3.0", {"start": v(94.08, 5.08) * mm, "end": v(93.63, 4.3) * mm});
            skLineSegment(sketch, "E163.0.4.0", {"start": v(92.63, 4.3) * mm, "end": v(92.18, 5.08) * mm});
            skLineSegment(sketch, "E163.3.4.0", {"start": v(92.18, 5.08) * mm, "end": v(93.08, 5.08) * mm});
            skLineSegment(sketch, "E163.6.4.0", {"start": v(92.63, 5.08) * mm, "end": v(92.63, 4.3) * mm, "construction": true});
            skLineSegment(sketch, "E163.9.4.0", {"start": v(93.08, 5.08) * mm, "end": v(92.63, 4.3) * mm});
            skLineSegment(sketch, "E163.0.5.0", {"start": v(91.63, 4.3) * mm, "end": v(91.18, 5.08) * mm});
            skLineSegment(sketch, "E163.3.5.0", {"start": v(91.18, 5.08) * mm, "end": v(92.08, 5.08) * mm});
            skLineSegment(sketch, "E163.6.5.0", {"start": v(91.63, 5.08) * mm, "end": v(91.63, 4.3) * mm, "construction": true});
            skLineSegment(sketch, "E163.9.5.0", {"start": v(92.08, 5.08) * mm, "end": v(91.63, 4.3) * mm});
            skLineSegment(sketch, "E163.0.6.0", {"start": v(90.63, 4.3) * mm, "end": v(90.18, 5.08) * mm});
            skLineSegment(sketch, "E163.3.6.0", {"start": v(90.18, 5.08) * mm, "end": v(91.08, 5.08) * mm});
            skLineSegment(sketch, "E163.6.6.0", {"start": v(90.63, 5.08) * mm, "end": v(90.63, 4.3) * mm, "construction": true});
            skLineSegment(sketch, "E163.9.6.0", {"start": v(91.08, 5.08) * mm, "end": v(90.63, 4.3) * mm});
            skLineSegment(sketch, "E163.0.7.0", {"start": v(89.63, 4.3) * mm, "end": v(89.18, 5.08) * mm});
            skLineSegment(sketch, "E163.3.7.0", {"start": v(89.18, 5.08) * mm, "end": v(90.08, 5.08) * mm});
            skLineSegment(sketch, "E163.6.7.0", {"start": v(89.63, 5.08) * mm, "end": v(89.63, 4.3) * mm, "construction": true});
            skLineSegment(sketch, "E163.9.7.0", {"start": v(90.08, 5.08) * mm, "end": v(89.63, 4.3) * mm});
            skLineSegment(sketch, "E163.0.8.0", {"start": v(88.63, 4.3) * mm, "end": v(88.18, 5.08) * mm});
            skLineSegment(sketch, "E163.3.8.0", {"start": v(88.18, 5.08) * mm, "end": v(89.08, 5.08) * mm});
            skLineSegment(sketch, "E163.6.8.0", {"start": v(88.63, 5.08) * mm, "end": v(88.63, 4.3) * mm, "construction": true});
            skLineSegment(sketch, "E163.9.8.0", {"start": v(89.08, 5.08) * mm, "end": v(88.63, 4.3) * mm});
            skLineSegment(sketch, "E163.0.9.0", {"start": v(87.63, 4.3) * mm, "end": v(87.18, 5.08) * mm});
            skLineSegment(sketch, "E163.3.9.0", {"start": v(87.18, 5.08) * mm, "end": v(88.08, 5.08) * mm});
            skLineSegment(sketch, "E163.6.9.0", {"start": v(87.63, 5.08) * mm, "end": v(87.63, 4.3) * mm, "construction": true});
            skLineSegment(sketch, "E163.9.9.0", {"start": v(88.08, 5.08) * mm, "end": v(87.63, 4.3) * mm});
            skLineSegment(sketch, "E163.0.10.0", {"start": v(86.63, 4.3) * mm, "end": v(86.18, 5.08) * mm});
            skLineSegment(sketch, "E163.3.10.0", {"start": v(86.18, 5.08) * mm, "end": v(87.08, 5.08) * mm});
            skLineSegment(sketch, "E163.6.10.0", {"start": v(86.63, 5.08) * mm, "end": v(86.63, 4.3) * mm, "construction": true});
            skLineSegment(sketch, "E163.9.10.0", {"start": v(87.08, 5.08) * mm, "end": v(86.63, 4.3) * mm});
            skLineSegment(sketch, "E163.0.11.0", {"start": v(85.63, 4.3) * mm, "end": v(85.18, 5.08) * mm});
            skLineSegment(sketch, "E163.3.11.0", {"start": v(85.18, 5.08) * mm, "end": v(86.08, 5.08) * mm});
            skLineSegment(sketch, "E163.6.11.0", {"start": v(85.63, 5.08) * mm, "end": v(85.63, 4.3) * mm, "construction": true});
            skLineSegment(sketch, "E163.9.11.0", {"start": v(86.08, 5.08) * mm, "end": v(85.63, 4.3) * mm});
            skLineSegment(sketch, "E163.0.12.0", {"start": v(84.63, 4.3) * mm, "end": v(84.18, 5.08) * mm});
            skLineSegment(sketch, "E163.3.12.0", {"start": v(84.18, 5.08) * mm, "end": v(85.08, 5.08) * mm});
            skLineSegment(sketch, "E163.6.12.0", {"start": v(84.63, 5.08) * mm, "end": v(84.63, 4.3) * mm, "construction": true});
            skLineSegment(sketch, "E163.9.12.0", {"start": v(85.08, 5.08) * mm, "end": v(84.63, 4.3) * mm});
            skLineSegment(sketch, "E163.0.13.0", {"start": v(83.63, 4.3) * mm, "end": v(83.18, 5.08) * mm});
            skLineSegment(sketch, "E163.3.13.0", {"start": v(83.18, 5.08) * mm, "end": v(84.08, 5.08) * mm});
            skLineSegment(sketch, "E163.6.13.0", {"start": v(83.63, 5.08) * mm, "end": v(83.63, 4.3) * mm, "construction": true});
            skLineSegment(sketch, "E163.9.13.0", {"start": v(84.08, 5.08) * mm, "end": v(83.63, 4.3) * mm});
            skLineSegment(sketch, "E163.0.14.0", {"start": v(82.63, 4.3) * mm, "end": v(82.18, 5.08) * mm});
            skLineSegment(sketch, "E163.3.14.0", {"start": v(82.18, 5.08) * mm, "end": v(83.08, 5.08) * mm});
            skLineSegment(sketch, "E163.6.14.0", {"start": v(82.63, 5.08) * mm, "end": v(82.63, 4.3) * mm, "construction": true});
            skLineSegment(sketch, "E163.9.14.0", {"start": v(83.08, 5.08) * mm, "end": v(82.63, 4.3) * mm});
            skLineSegment(sketch, "E163.0.15.0", {"start": v(81.63, 4.3) * mm, "end": v(81.18, 5.08) * mm});
            skLineSegment(sketch, "E163.3.15.0", {"start": v(81.18, 5.08) * mm, "end": v(82.08, 5.08) * mm});
            skLineSegment(sketch, "E163.6.15.0", {"start": v(81.63, 5.08) * mm, "end": v(81.63, 4.3) * mm, "construction": true});
            skLineSegment(sketch, "E163.9.15.0", {"start": v(82.08, 5.08) * mm, "end": v(81.63, 4.3) * mm});
            skLineSegment(sketch, "E163.0.16.0", {"start": v(80.63, 4.3) * mm, "end": v(80.18, 5.08) * mm});
            skLineSegment(sketch, "E163.3.16.0", {"start": v(80.18, 5.08) * mm, "end": v(81.08, 5.08) * mm});
            skLineSegment(sketch, "E163.6.16.0", {"start": v(80.63, 5.08) * mm, "end": v(80.63, 4.3) * mm, "construction": true});
            skLineSegment(sketch, "E163.9.16.0", {"start": v(81.08, 5.08) * mm, "end": v(80.63, 4.3) * mm});
            skLineSegment(sketch, "E163.0.17.0", {"start": v(79.63, 4.3) * mm, "end": v(79.18, 5.08) * mm});
            skLineSegment(sketch, "E163.3.17.0", {"start": v(79.18, 5.08) * mm, "end": v(80.08, 5.08) * mm});
            skLineSegment(sketch, "E163.6.17.0", {"start": v(79.63, 5.08) * mm, "end": v(79.63, 4.3) * mm, "construction": true});
            skLineSegment(sketch, "E163.9.17.0", {"start": v(80.08, 5.08) * mm, "end": v(79.63, 4.3) * mm});
            skLineSegment(sketch, "E163.0.18.0", {"start": v(78.63, 4.3) * mm, "end": v(78.18, 5.08) * mm});
            skLineSegment(sketch, "E163.3.18.0", {"start": v(78.18, 5.08) * mm, "end": v(79.08, 5.08) * mm});
            skLineSegment(sketch, "E163.6.18.0", {"start": v(78.63, 5.08) * mm, "end": v(78.63, 4.3) * mm, "construction": true});
            skLineSegment(sketch, "E163.9.18.0", {"start": v(79.08, 5.08) * mm, "end": v(78.63, 4.3) * mm});
            skLineSegment(sketch, "E163.0.19.0", {"start": v(77.63, 4.3) * mm, "end": v(77.18, 5.08) * mm});
            skLineSegment(sketch, "E163.3.19.0", {"start": v(77.18, 5.08) * mm, "end": v(78.08, 5.08) * mm});
            skLineSegment(sketch, "E163.6.19.0", {"start": v(77.63, 5.08) * mm, "end": v(77.63, 4.3) * mm, "construction": true});
            skLineSegment(sketch, "E163.9.19.0", {"start": v(78.08, 5.08) * mm, "end": v(77.63, 4.3) * mm});
            skLineSegment(sketch, "E164.MirrorCS", {"start": v(-90.63, 5.08) * mm, "end": v(-90.63, 4.3) * mm});
            skLineSegment(sketch, "E165.MirrorCS", {"start": v(-87.63, 5.08) * mm, "end": v(-87.63, 4.3) * mm});
            skLineSegment(sketch, "E166.MirrorCS", {"start": v(-91.63, 5.08) * mm, "end": v(-91.63, 4.3) * mm});
            skLineSegment(sketch, "E167.MirrorCS", {"start": v(-94.63, 5.08) * mm, "end": v(-94.63, 4.3) * mm});
            skLineSegment(sketch, "E168.MirrorCS", {"start": v(-90.63, 4.3) * mm, "end": v(-90.18, 5.08) * mm});
            skLineSegment(sketch, "E169.MirrorCS", {"start": v(-92.63, 5.08) * mm, "end": v(-92.63, 4.3) * mm});
            skLineSegment(sketch, "E170.MirrorCS", {"start": v(-93.63, 5.08) * mm, "end": v(-93.63, 4.3) * mm});
            skLineSegment(sketch, "E171.MirrorCS", {"start": v(-89.63, 5.08) * mm, "end": v(-89.63, 4.3) * mm});
            skLineSegment(sketch, "E172.MirrorCS", {"start": v(-83.63, 5.08) * mm, "end": v(-83.63, 4.3) * mm});
            skLineSegment(sketch, "E173.MirrorCS", {"start": v(-90.18, 5.08) * mm, "end": v(-91.08, 5.08) * mm});
            skLineSegment(sketch, "E174.MirrorCS", {"start": v(-88.63, 5.08) * mm, "end": v(-88.63, 4.3) * mm});
            skLineSegment(sketch, "E175.MirrorCS", {"start": v(-84.63, 5.08) * mm, "end": v(-84.63, 4.3) * mm});
            skLineSegment(sketch, "E176.MirrorCS", {"start": v(-92.18, 5.08) * mm, "end": v(-93.08, 5.08) * mm});
            skLineSegment(sketch, "E177.MirrorCS", {"start": v(-95.63, 5.08) * mm, "end": v(-95.63, 4.3) * mm});
            skLineSegment(sketch, "E178.MirrorCS", {"start": v(-87.63, 4.3) * mm, "end": v(-87.18, 5.08) * mm});
            skLineSegment(sketch, "E179.MirrorCS", {"start": v(-91.63, 4.3) * mm, "end": v(-91.18, 5.08) * mm});
            skLineSegment(sketch, "E180.MirrorCS", {"start": v(-85.63, 5.08) * mm, "end": v(-85.63, 4.3) * mm});
            skLineSegment(sketch, "E181.MirrorCS", {"start": v(-95.18, 5.08) * mm, "end": v(-96.08, 5.08) * mm});
            skLineSegment(sketch, "E182.MirrorCS", {"start": v(-93.18, 5.08) * mm, "end": v(-94.08, 5.08) * mm});
            skLineSegment(sketch, "E183.MirrorCS", {"start": v(-86.63, 5.08) * mm, "end": v(-86.63, 4.3) * mm});
            skLineSegment(sketch, "E184.MirrorCS", {"start": v(-82.63, 5.08) * mm, "end": v(-82.63, 4.3) * mm});
            skLineSegment(sketch, "E185.MirrorCS", {"start": v(-93.63, 4.3) * mm, "end": v(-93.18, 5.08) * mm});
            skLineSegment(sketch, "E186.MirrorCS", {"start": v(-89.63, 4.3) * mm, "end": v(-89.18, 5.08) * mm});
            skLineSegment(sketch, "E187.MirrorCS", {"start": v(-94.63, 4.3) * mm, "end": v(-94.18, 5.08) * mm});
            skLineSegment(sketch, "E188.MirrorCS", {"start": v(-82.63, 4.3) * mm, "end": v(-82.18, 5.08) * mm});
            skLineSegment(sketch, "E189.MirrorCS", {"start": v(-86.63, 4.3) * mm, "end": v(-86.18, 5.08) * mm});
            skLineSegment(sketch, "E190.MirrorCS", {"start": v(-96.08, 5.08) * mm, "end": v(-95.63, 4.3) * mm});
            skLineSegment(sketch, "E191.MirrorCS", {"start": v(-94.18, 5.08) * mm, "end": v(-95.08, 5.08) * mm});
            skLineSegment(sketch, "E192.MirrorCS", {"start": v(-93.08, 5.08) * mm, "end": v(-92.63, 4.3) * mm});
            skLineSegment(sketch, "E193.MirrorCS", {"start": v(-91.18, 5.08) * mm, "end": v(-92.08, 5.08) * mm});
            skLineSegment(sketch, "E194.MirrorCS", {"start": v(-87.18, 5.08) * mm, "end": v(-88.08, 5.08) * mm});
            skLineSegment(sketch, "E195.MirrorCS", {"start": v(-96.63, 5.08) * mm, "end": v(-96.63, 4.3) * mm});
            skLineSegment(sketch, "E196.MirrorCS", {"start": v(-88.63, 4.3) * mm, "end": v(-88.18, 5.08) * mm});
            skLineSegment(sketch, "E197.MirrorCS", {"start": v(-92.63, 4.3) * mm, "end": v(-92.18, 5.08) * mm});
            skLineSegment(sketch, "E198.MirrorCS", {"start": v(-84.18, 5.08) * mm, "end": v(-85.08, 5.08) * mm});
            skLineSegment(sketch, "E199.MirrorCS", {"start": v(-83.63, 4.3) * mm, "end": v(-83.18, 5.08) * mm});
            skLineSegment(sketch, "E200.MirrorCS", {"start": v(-91.08, 5.08) * mm, "end": v(-90.63, 4.3) * mm});
            skLineSegment(sketch, "E201.MirrorCS", {"start": v(-95.08, 5.08) * mm, "end": v(-94.63, 4.3) * mm});
            skLineSegment(sketch, "E202.MirrorCS", {"start": v(-81.63, 5.08) * mm, "end": v(-81.63, 4.3) * mm});
            skLineSegment(sketch, "E203.MirrorCS", {"start": v(-89.18, 5.08) * mm, "end": v(-90.08, 5.08) * mm});
            skLineSegment(sketch, "E204.MirrorCS", {"start": v(-92.08, 5.08) * mm, "end": v(-91.63, 4.3) * mm});
            skLineSegment(sketch, "E205.MirrorCS", {"start": v(-84.08, 5.08) * mm, "end": v(-83.63, 4.3) * mm});
            skLineSegment(sketch, "E206.MirrorCS", {"start": v(-85.63, 4.3) * mm, "end": v(-85.18, 5.08) * mm});
            skLineSegment(sketch, "E207.MirrorCS", {"start": v(-94.08, 5.08) * mm, "end": v(-93.63, 4.3) * mm});
            skLineSegment(sketch, "E208.MirrorCS", {"start": v(-90.08, 5.08) * mm, "end": v(-89.63, 4.3) * mm});
            skLineSegment(sketch, "E209.MirrorCS", {"start": v(-79.63, 5.08) * mm, "end": v(-79.63, 4.3) * mm});
            skLineSegment(sketch, "E210.MirrorCS", {"start": v(-89.08, 5.08) * mm, "end": v(-88.63, 4.3) * mm});
            skLineSegment(sketch, "E211.MirrorCS", {"start": v(-85.08, 5.08) * mm, "end": v(-84.63, 4.3) * mm});
            skLineSegment(sketch, "E212.MirrorCS", {"start": v(-80.63, 5.08) * mm, "end": v(-80.63, 4.3) * mm});
            skLineSegment(sketch, "E213.MirrorCS", {"start": v(-83.18, 5.08) * mm, "end": v(-84.08, 5.08) * mm});
            skLineSegment(sketch, "E214.MirrorCS", {"start": v(-86.08, 5.08) * mm, "end": v(-85.63, 4.3) * mm});
            skLineSegment(sketch, "E215.MirrorCS", {"start": v(-86.18, 5.08) * mm, "end": v(-87.08, 5.08) * mm});
            skLineSegment(sketch, "E216.MirrorCS", {"start": v(-96.63, 4.3) * mm, "end": v(-96.18, 5.08) * mm});
            skLineSegment(sketch, "E217.MirrorCS", {"start": v(-84.63, 4.3) * mm, "end": v(-84.18, 5.08) * mm});
            skLineSegment(sketch, "E218.MirrorCS", {"start": v(-88.18, 5.08) * mm, "end": v(-89.08, 5.08) * mm});
            skLineSegment(sketch, "E219.MirrorCS", {"start": v(-96.63, 4.3) * mm, "end": v(-95.63, 4.3) * mm});
            skLineSegment(sketch, "E220.MirrorCS", {"start": v(-85.18, 5.08) * mm, "end": v(-86.08, 5.08) * mm});
            skLineSegment(sketch, "E221.MirrorCS", {"start": v(-81.18, 5.08) * mm, "end": v(-82.08, 5.08) * mm});
            skLineSegment(sketch, "E222.MirrorCS", {"start": v(-78.63, 5.08) * mm, "end": v(-78.63, 4.3) * mm});
            skLineSegment(sketch, "E223.MirrorCS", {"start": v(-81.63, 4.3) * mm, "end": v(-81.18, 5.08) * mm});
            skLineSegment(sketch, "E224.MirrorCS", {"start": v(-87.08, 5.08) * mm, "end": v(-86.63, 4.3) * mm});
            skLineSegment(sketch, "E225.MirrorCS", {"start": v(-88.08, 5.08) * mm, "end": v(-87.63, 4.3) * mm});
            skLineSegment(sketch, "E226.MirrorCS", {"start": v(-83.08, 5.08) * mm, "end": v(-82.63, 4.3) * mm});
            skLineSegment(sketch, "E227.MirrorCS", {"start": v(-81.08, 5.08) * mm, "end": v(-80.63, 4.3) * mm});
            skLineSegment(sketch, "E228.MirrorCS", {"start": v(-95.63, 4.3) * mm, "end": v(-95.18, 5.08) * mm});
            skLineSegment(sketch, "E229.MirrorCS", {"start": v(-78.18, 5.08) * mm, "end": v(-79.08, 5.08) * mm});
            skLineSegment(sketch, "E230.MirrorCS", {"start": v(-82.18, 5.08) * mm, "end": v(-83.08, 5.08) * mm});
            skLineSegment(sketch, "E231.MirrorCS", {"start": v(-96.18, 5.08) * mm, "end": v(-97.08, 5.08) * mm});
            skLineSegment(sketch, "E232.MirrorCS", {"start": v(-80.18, 5.08) * mm, "end": v(-81.08, 5.08) * mm});
            skLineSegment(sketch, "E233.MirrorCS", {"start": v(-79.63, 4.3) * mm, "end": v(-79.18, 5.08) * mm});
            skLineSegment(sketch, "E234.MirrorCS", {"start": v(-82.08, 5.08) * mm, "end": v(-81.63, 4.3) * mm});
            skLineSegment(sketch, "E235.MirrorCS", {"start": v(-78.63, 4.3) * mm, "end": v(-78.18, 5.08) * mm});
            skLineSegment(sketch, "E236.MirrorCS", {"start": v(-79.18, 5.08) * mm, "end": v(-80.08, 5.08) * mm});
            skLineSegment(sketch, "E237.MirrorCS", {"start": v(-80.63, 4.3) * mm, "end": v(-80.18, 5.08) * mm});
            skLineSegment(sketch, "E238.MirrorCS", {"start": v(-77.63, 5.08) * mm, "end": v(-77.63, 4.3) * mm});
            skLineSegment(sketch, "E239.MirrorCS", {"start": v(-79.08, 5.08) * mm, "end": v(-78.63, 4.3) * mm});
            skLineSegment(sketch, "E240.MirrorCS", {"start": v(-80.08, 5.08) * mm, "end": v(-79.63, 4.3) * mm});
            skLineSegment(sketch, "E241.MirrorCS", {"start": v(-77.18, 5.08) * mm, "end": v(-78.08, 5.08) * mm});
            skLineSegment(sketch, "E242.MirrorCS", {"start": v(-78.08, 5.08) * mm, "end": v(-77.63, 4.3) * mm});
            skLineSegment(sketch, "E243.MirrorCS", {"start": v(-97.08, 5.08) * mm, "end": v(-96.63, 4.3) * mm});
            skLineSegment(sketch, "E244.MirrorCS", {"start": v(-77.63, 4.3) * mm, "end": v(-77.18, 5.08) * mm});
            skSolve(sketch);
        }
        {
            var Q0;
            Q0 = qSketchRegion(id + "F15", true);
            var Q1;
            Q1=sQuery(id+"F15.wireOp",EDGE,"E118");
            revolve(context, id + "F16", {"operationType" : NewBodyOperationType.REMOVE, "entities" : qUnion([Q0]), "axis" : qUnion([Q1]), "revolveType" : RevolveType.FULL, "oppositeDirection" : true});
        }
    });
